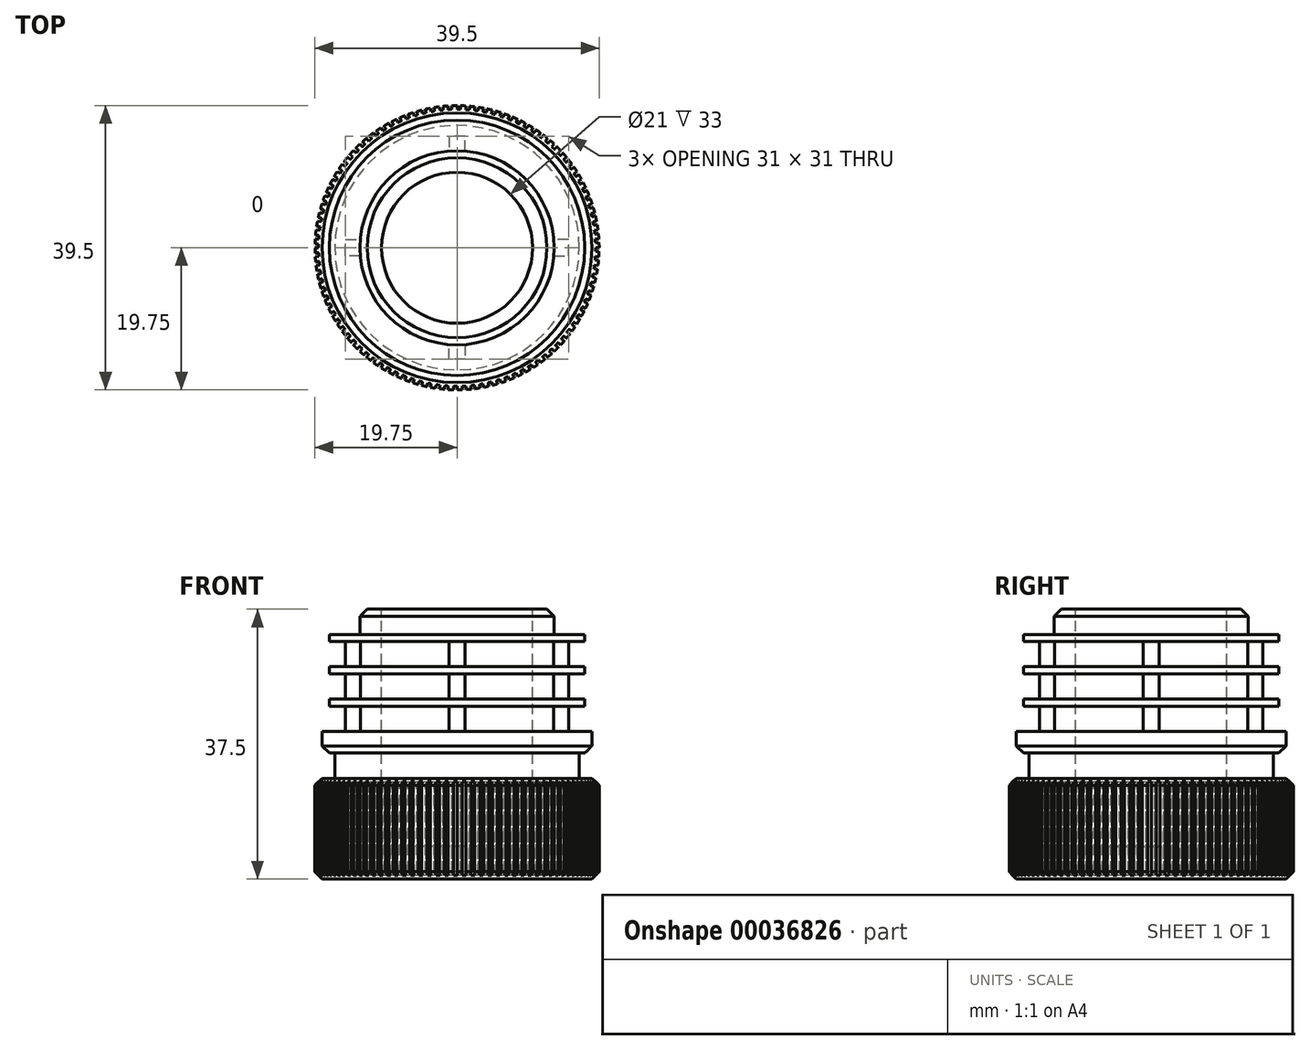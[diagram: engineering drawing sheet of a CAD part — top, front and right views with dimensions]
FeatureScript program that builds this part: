
annotation { "Feature Type Name" : "Feature", "Feature Type Description" : "" }
export const myFeature = defineFeature(function(context is Context, id is Id, definition is map)
    precondition{}
    {
        {
            var Q0;
            Q0=qCreatedBy(makeId("Front.planeOp"),FACE);
            var sketch = newSketch(context, id + "F0", { "sketchPlane" : qUnion([Q0])});
            skLineSegment(sketch, "E0", {"start": v(0, 48.86) * mm, "end": v(0, -30.6) * mm, "construction": true});
            skLineSegment(sketch, "E1", {"start": v(19.75, 0) * mm, "end": v(19.75, 14) * mm});
            skLineSegment(sketch, "E2", {"start": v(19.75, 14) * mm, "end": v(17, 14) * mm});
            skLineSegment(sketch, "E3", {"start": v(17, 14) * mm, "end": v(17, 17.5) * mm});
            skLineSegment(sketch, "E4", {"start": v(17, 17.5) * mm, "end": v(18.75, 17.5) * mm});
            skLineSegment(sketch, "E5", {"start": v(18.75, 17.5) * mm, "end": v(18.75, 20.5) * mm});
            skLineSegment(sketch, "E6", {"start": v(18.75, 20.5) * mm, "end": v(13.5, 20.5) * mm});
            skLineSegment(sketch, "E7", {"start": v(13.5, 20.5) * mm, "end": v(13.5, 24) * mm});
            skLineSegment(sketch, "E8", {"start": v(13.5, 24) * mm, "end": v(17.75, 24) * mm});
            skLineSegment(sketch, "E9", {"start": v(17.75, 24) * mm, "end": v(17.75, 25) * mm});
            skLineSegment(sketch, "E10", {"start": v(17.75, 25) * mm, "end": v(13.5, 25) * mm});
            skLineSegment(sketch, "E11", {"start": v(13.5, 25) * mm, "end": v(13.5, 28.5) * mm});
            skLineSegment(sketch, "E12", {"start": v(13.5, 28.5) * mm, "end": v(17.75, 28.5) * mm});
            skLineSegment(sketch, "E13", {"start": v(17.75, 28.5) * mm, "end": v(17.75, 29.5) * mm});
            skLineSegment(sketch, "E14", {"start": v(17.75, 29.5) * mm, "end": v(13.5, 29.5) * mm});
            skLineSegment(sketch, "E15", {"start": v(13.5, 29.5) * mm, "end": v(13.5, 33) * mm});
            skLineSegment(sketch, "E16", {"start": v(13.5, 33) * mm, "end": v(17.75, 33) * mm});
            skLineSegment(sketch, "E17", {"start": v(17.75, 33) * mm, "end": v(17.75, 34) * mm});
            skLineSegment(sketch, "E18", {"start": v(17.75, 34) * mm, "end": v(13.5, 34) * mm});
            skLineSegment(sketch, "E19", {"start": v(13.5, 34) * mm, "end": v(13.5, 37.5) * mm});
            skLineSegment(sketch, "E20", {"start": v(13.5, 37.5) * mm, "end": v(0, 37.5) * mm});
            skLineSegment(sketch, "E21", {"start": v(0, 37.5) * mm, "end": v(0, 0) * mm});
            skLineSegment(sketch, "E22", {"start": v(0, 0) * mm, "end": v(19.75, 0) * mm});
            skSolve(sketch);
        }
        {
            var Q0;
            Q0=makeQuery(id+"F0.imprint","IMPRINT",FACE,{"disambiguationData":[TD([[makeQuery(id+"F0.imprint","IMPRINT",EDGE,{"derivedFrom":sQuery(id+"F0.wireOp",EDGE,"E1")}),1.0]])]});
            var Q1;
            Q1=sQuery(id+"F0.wireOp",EDGE,"E21");
            revolve(context, id + "F1", {"entities" : qUnion([Q0]), "axis" : qUnion([Q1]), "revolveType" : RevolveType.FULL});
        }
        {
            var Q0;
            Q0=makeQuery(id+"F1.opRevolve","SWEPT_FACE",FACE,{"disambiguationData":[OSD([sQuery(id+"F0.wireOp",EDGE,"E20")])]});
            var sketch = newSketch(context, id + "F2", { "sketchPlane" : qUnion([Q0])});
            skCircle(sketch, "E23.0", {"center": v(0, 0) * mm, "radius": 13.5 * mm});
            skCircle(sketch, "E24.1", {"center": v(0, 0) * mm, "radius": 19.75 * mm});
            skLineSegment(sketch, "E25", {"start": v(-1.12, -13.45) * mm, "end": v(-1.12, -15.5) * mm});
            skLineSegment(sketch, "E26", {"start": v(-1.12, -15.5) * mm, "end": v(1.13, -15.5) * mm});
            skLineSegment(sketch, "E27", {"start": v(1.13, -15.5) * mm, "end": v(1.13, -13.45) * mm});
            skLineSegment(sketch, "E28", {"start": v(-35.88, 0) * mm, "end": v(36.7, 0) * mm, "construction": true});
            skLineSegment(sketch, "E29", {"start": v(0, 33.46) * mm, "end": v(0, -30.14) * mm, "construction": true});
            skPoint(sketch, "E30", {"position": v(0, -15.5) * mm});
            skLineSegment(sketch, "E31.MirrorCS", {"start": v(-1.13, 13.45) * mm, "end": v(-1.13, 15.5) * mm});
            skLineSegment(sketch, "E32.MirrorCS", {"start": v(1.12, 15.5) * mm, "end": v(1.12, 13.45) * mm});
            skLineSegment(sketch, "E33.MirrorCS", {"start": v(-1.12, 15.5) * mm, "end": v(1.13, 15.5) * mm});
            skLineSegment(sketch, "E34.1.0", {"start": v(-13.45, 1.12) * mm, "end": v(-15.5, 1.12) * mm});
            skLineSegment(sketch, "E34.1.1", {"start": v(-15.5, 1.12) * mm, "end": v(-15.5, -1.13) * mm});
            skLineSegment(sketch, "E34.1.2", {"start": v(-15.5, -1.13) * mm, "end": v(-13.45, -1.13) * mm});
            skLineSegment(sketch, "E34.1.3", {"start": v(15.5, 1.12) * mm, "end": v(15.5, -1.13) * mm});
            skLineSegment(sketch, "E34.1.4", {"start": v(13.45, 1.13) * mm, "end": v(15.5, 1.13) * mm});
            skLineSegment(sketch, "E34.1.5", {"start": v(15.5, -1.12) * mm, "end": v(13.45, -1.12) * mm});
            skLineSegment(sketch, "E34.anchor1", {"start": v(0, 0) * mm, "end": v(-1.12, -15.5) * mm, "construction": true});
            skLineSegment(sketch, "E34.anchor2", {"start": v(0, 0) * mm, "end": v(-15.5, 1.12) * mm, "construction": true});
            skLineSegment(sketch, "E35", {"start": v(0, -19.75) * mm, "end": v(0, -19.25) * mm});
            skLineSegment(sketch, "E36", {"start": v(0, -19.25) * mm, "end": v(-0.5, -19.25) * mm});
            skLineSegment(sketch, "E37", {"start": v(-0.5, -19.25) * mm, "end": v(-0.5, -19.74) * mm});
            skLineSegment(sketch, "E38.1.0", {"start": v(0.7, -19.24) * mm, "end": v(0.74, -19.74) * mm});
            skLineSegment(sketch, "E38.1.1", {"start": v(1.2, -19.21) * mm, "end": v(0.7, -19.24) * mm});
            skLineSegment(sketch, "E38.1.2", {"start": v(1.24, -19.71) * mm, "end": v(1.2, -19.21) * mm});
            skLineSegment(sketch, "E38.2.0", {"start": v(1.92, -19.16) * mm, "end": v(1.98, -19.65) * mm});
            skLineSegment(sketch, "E38.2.1", {"start": v(2.41, -19.1) * mm, "end": v(1.92, -19.16) * mm});
            skLineSegment(sketch, "E38.2.2", {"start": v(2.48, -19.6) * mm, "end": v(2.41, -19.1) * mm});
            skLineSegment(sketch, "E38.3.0", {"start": v(3.12, -19) * mm, "end": v(3.2, -19.49) * mm});
            skLineSegment(sketch, "E38.3.1", {"start": v(3.6, -18.9) * mm, "end": v(3.12, -19) * mm});
            skLineSegment(sketch, "E38.3.2", {"start": v(3.7, -19.4) * mm, "end": v(3.6, -18.9) * mm});
            skLineSegment(sketch, "E38.4.0", {"start": v(4.3, -18.77) * mm, "end": v(4.43, -19.25) * mm});
            skLineSegment(sketch, "E38.4.1", {"start": v(4.79, -18.65) * mm, "end": v(4.3, -18.77) * mm});
            skLineSegment(sketch, "E38.4.2", {"start": v(4.91, -19.13) * mm, "end": v(4.79, -18.65) * mm});
            skLineSegment(sketch, "E38.5.0", {"start": v(5.47, -18.46) * mm, "end": v(5.63, -18.93) * mm});
            skLineSegment(sketch, "E38.5.1", {"start": v(5.95, -18.3) * mm, "end": v(5.47, -18.46) * mm});
            skLineSegment(sketch, "E38.5.2", {"start": v(6.1, -18.78) * mm, "end": v(5.95, -18.3) * mm});
            skLineSegment(sketch, "E38.6.0", {"start": v(6.62, -18.08) * mm, "end": v(6.8, -18.54) * mm});
            skLineSegment(sketch, "E38.6.1", {"start": v(7.09, -17.9) * mm, "end": v(6.62, -18.08) * mm});
            skLineSegment(sketch, "E38.6.2", {"start": v(7.27, -18.36) * mm, "end": v(7.09, -17.9) * mm});
            skLineSegment(sketch, "E38.7.0", {"start": v(7.74, -17.63) * mm, "end": v(7.95, -18.08) * mm});
            skLineSegment(sketch, "E38.7.1", {"start": v(8.2, -17.42) * mm, "end": v(7.74, -17.63) * mm});
            skLineSegment(sketch, "E38.7.2", {"start": v(8.4, -17.87) * mm, "end": v(8.2, -17.42) * mm});
            skLineSegment(sketch, "E38.8.0", {"start": v(8.84, -17.1) * mm, "end": v(9.07, -17.54) * mm});
            skLineSegment(sketch, "E38.8.1", {"start": v(9.27, -16.87) * mm, "end": v(8.84, -17.1) * mm});
            skLineSegment(sketch, "E38.8.2", {"start": v(9.51, -17.3) * mm, "end": v(9.27, -16.87) * mm});
            skLineSegment(sketch, "E38.9.0", {"start": v(9.9, -16.52) * mm, "end": v(10.16, -16.94) * mm});
            skLineSegment(sketch, "E38.9.1", {"start": v(10.31, -16.25) * mm, "end": v(9.9, -16.52) * mm});
            skLineSegment(sketch, "E38.9.2", {"start": v(10.58, -16.68) * mm, "end": v(10.31, -16.25) * mm});
            skLineSegment(sketch, "E38.10.0", {"start": v(10.91, -15.87) * mm, "end": v(11.2, -16.27) * mm});
            skLineSegment(sketch, "E38.10.1", {"start": v(11.31, -15.57) * mm, "end": v(10.91, -15.87) * mm});
            skLineSegment(sketch, "E38.10.2", {"start": v(11.6, -15.98) * mm, "end": v(11.31, -15.57) * mm});
            skLineSegment(sketch, "E38.11.0", {"start": v(11.89, -15.15) * mm, "end": v(12.2, -15.53) * mm});
            skLineSegment(sketch, "E38.11.1", {"start": v(12.27, -14.83) * mm, "end": v(11.89, -15.15) * mm});
            skLineSegment(sketch, "E38.11.2", {"start": v(12.59, -15.22) * mm, "end": v(12.27, -14.83) * mm});
            skLineSegment(sketch, "E38.12.0", {"start": v(12.81, -14.37) * mm, "end": v(13.15, -14.73) * mm});
            skLineSegment(sketch, "E38.12.1", {"start": v(13.18, -14.03) * mm, "end": v(12.81, -14.37) * mm});
            skLineSegment(sketch, "E38.12.2", {"start": v(13.52, -14.4) * mm, "end": v(13.18, -14.03) * mm});
            skLineSegment(sketch, "E38.13.0", {"start": v(13.7, -13.54) * mm, "end": v(14.05, -13.88) * mm});
            skLineSegment(sketch, "E38.13.1", {"start": v(14.03, -13.18) * mm, "end": v(13.7, -13.54) * mm});
            skLineSegment(sketch, "E38.13.2", {"start": v(14.4, -13.52) * mm, "end": v(14.03, -13.18) * mm});
            skLineSegment(sketch, "E38.14.0", {"start": v(14.51, -12.66) * mm, "end": v(14.9, -12.97) * mm});
            skLineSegment(sketch, "E38.14.1", {"start": v(14.83, -12.27) * mm, "end": v(14.51, -12.66) * mm});
            skLineSegment(sketch, "E38.14.2", {"start": v(15.22, -12.59) * mm, "end": v(14.83, -12.27) * mm});
            skLineSegment(sketch, "E38.15.0", {"start": v(15.28, -11.72) * mm, "end": v(15.68, -12) * mm});
            skLineSegment(sketch, "E38.15.1", {"start": v(15.57, -11.31) * mm, "end": v(15.28, -11.72) * mm});
            skLineSegment(sketch, "E38.15.2", {"start": v(15.98, -11.6) * mm, "end": v(15.57, -11.31) * mm});
            skLineSegment(sketch, "E38.16.0", {"start": v(15.99, -10.74) * mm, "end": v(16.4, -11) * mm});
            skLineSegment(sketch, "E38.16.1", {"start": v(16.25, -10.31) * mm, "end": v(15.99, -10.74) * mm});
            skLineSegment(sketch, "E38.16.2", {"start": v(16.68, -10.58) * mm, "end": v(16.25, -10.31) * mm});
            skLineSegment(sketch, "E38.17.0", {"start": v(16.63, -9.71) * mm, "end": v(17.06, -9.95) * mm});
            skLineSegment(sketch, "E38.17.1", {"start": v(16.87, -9.27) * mm, "end": v(16.63, -9.71) * mm});
            skLineSegment(sketch, "E38.17.2", {"start": v(17.3, -9.51) * mm, "end": v(16.87, -9.27) * mm});
            skLineSegment(sketch, "E38.18.0", {"start": v(17.2, -8.65) * mm, "end": v(17.65, -8.86) * mm});
            skLineSegment(sketch, "E38.18.1", {"start": v(17.42, -8.2) * mm, "end": v(17.2, -8.65) * mm});
            skLineSegment(sketch, "E38.18.2", {"start": v(17.87, -8.4) * mm, "end": v(17.42, -8.2) * mm});
            skLineSegment(sketch, "E38.19.0", {"start": v(17.71, -7.55) * mm, "end": v(18.17, -7.73) * mm});
            skLineSegment(sketch, "E38.19.1", {"start": v(17.9, -7.09) * mm, "end": v(17.71, -7.55) * mm});
            skLineSegment(sketch, "E38.19.2", {"start": v(18.36, -7.27) * mm, "end": v(17.9, -7.09) * mm});
            skLineSegment(sketch, "E38.20.0", {"start": v(18.15, -6.42) * mm, "end": v(18.62, -6.58) * mm});
            skLineSegment(sketch, "E38.20.1", {"start": v(18.3, -5.95) * mm, "end": v(18.15, -6.42) * mm});
            skLineSegment(sketch, "E38.20.2", {"start": v(18.78, -6.1) * mm, "end": v(18.3, -5.95) * mm});
            skLineSegment(sketch, "E38.21.0", {"start": v(18.52, -5.27) * mm, "end": v(19, -5.4) * mm});
            skLineSegment(sketch, "E38.21.1", {"start": v(18.65, -4.79) * mm, "end": v(18.52, -5.27) * mm});
            skLineSegment(sketch, "E38.21.2", {"start": v(19.13, -4.91) * mm, "end": v(18.65, -4.79) * mm});
            skLineSegment(sketch, "E38.22.0", {"start": v(18.82, -4.1) * mm, "end": v(19.3, -4.2) * mm});
            skLineSegment(sketch, "E38.22.1", {"start": v(18.9, -3.6) * mm, "end": v(18.82, -4.1) * mm});
            skLineSegment(sketch, "E38.22.2", {"start": v(19.4, -3.7) * mm, "end": v(18.9, -3.6) * mm});
            skLineSegment(sketch, "E38.23.0", {"start": v(19.04, -2.9) * mm, "end": v(19.53, -2.97) * mm});
            skLineSegment(sketch, "E38.23.1", {"start": v(19.1, -2.41) * mm, "end": v(19.04, -2.9) * mm});
            skLineSegment(sketch, "E38.23.2", {"start": v(19.6, -2.48) * mm, "end": v(19.1, -2.41) * mm});
            skLineSegment(sketch, "E38.24.0", {"start": v(19.18, -1.7) * mm, "end": v(19.67, -1.74) * mm});
            skLineSegment(sketch, "E38.24.1", {"start": v(19.21, -1.2) * mm, "end": v(19.18, -1.7) * mm});
            skLineSegment(sketch, "E38.24.2", {"start": v(19.71, -1.24) * mm, "end": v(19.21, -1.2) * mm});
            skLineSegment(sketch, "E38.25.0", {"start": v(19.25, -0.5) * mm, "end": v(19.74, -0.5) * mm});
            skLineSegment(sketch, "E38.25.1", {"start": v(19.25, 0) * mm, "end": v(19.25, -0.5) * mm});
            skLineSegment(sketch, "E38.25.2", {"start": v(19.75, 0) * mm, "end": v(19.25, 0) * mm});
            skLineSegment(sketch, "E38.26.0", {"start": v(19.24, 0.7) * mm, "end": v(19.74, 0.74) * mm});
            skLineSegment(sketch, "E38.26.1", {"start": v(19.21, 1.2) * mm, "end": v(19.24, 0.7) * mm});
            skLineSegment(sketch, "E38.26.2", {"start": v(19.71, 1.24) * mm, "end": v(19.21, 1.2) * mm});
            skLineSegment(sketch, "E38.27.0", {"start": v(19.16, 1.92) * mm, "end": v(19.65, 1.98) * mm});
            skLineSegment(sketch, "E38.27.1", {"start": v(19.1, 2.41) * mm, "end": v(19.16, 1.92) * mm});
            skLineSegment(sketch, "E38.27.2", {"start": v(19.6, 2.48) * mm, "end": v(19.1, 2.41) * mm});
            skLineSegment(sketch, "E38.28.0", {"start": v(19, 3.12) * mm, "end": v(19.49, 3.2) * mm});
            skLineSegment(sketch, "E38.28.1", {"start": v(18.9, 3.6) * mm, "end": v(19, 3.12) * mm});
            skLineSegment(sketch, "E38.28.2", {"start": v(19.4, 3.7) * mm, "end": v(18.9, 3.6) * mm});
            skLineSegment(sketch, "E38.29.0", {"start": v(18.77, 4.3) * mm, "end": v(19.25, 4.43) * mm});
            skLineSegment(sketch, "E38.29.1", {"start": v(18.65, 4.79) * mm, "end": v(18.77, 4.3) * mm});
            skLineSegment(sketch, "E38.29.2", {"start": v(19.13, 4.91) * mm, "end": v(18.65, 4.79) * mm});
            skLineSegment(sketch, "E38.30.0", {"start": v(18.46, 5.47) * mm, "end": v(18.93, 5.63) * mm});
            skLineSegment(sketch, "E38.30.1", {"start": v(18.3, 5.95) * mm, "end": v(18.46, 5.47) * mm});
            skLineSegment(sketch, "E38.30.2", {"start": v(18.78, 6.1) * mm, "end": v(18.3, 5.95) * mm});
            skLineSegment(sketch, "E38.31.0", {"start": v(18.08, 6.62) * mm, "end": v(18.54, 6.8) * mm});
            skLineSegment(sketch, "E38.31.1", {"start": v(17.9, 7.09) * mm, "end": v(18.08, 6.62) * mm});
            skLineSegment(sketch, "E38.31.2", {"start": v(18.36, 7.27) * mm, "end": v(17.9, 7.09) * mm});
            skLineSegment(sketch, "E38.32.0", {"start": v(17.63, 7.74) * mm, "end": v(18.08, 7.95) * mm});
            skLineSegment(sketch, "E38.32.1", {"start": v(17.42, 8.2) * mm, "end": v(17.63, 7.74) * mm});
            skLineSegment(sketch, "E38.32.2", {"start": v(17.87, 8.4) * mm, "end": v(17.42, 8.2) * mm});
            skLineSegment(sketch, "E38.33.0", {"start": v(17.1, 8.84) * mm, "end": v(17.54, 9.07) * mm});
            skLineSegment(sketch, "E38.33.1", {"start": v(16.87, 9.27) * mm, "end": v(17.1, 8.84) * mm});
            skLineSegment(sketch, "E38.33.2", {"start": v(17.3, 9.51) * mm, "end": v(16.87, 9.27) * mm});
            skLineSegment(sketch, "E38.34.0", {"start": v(16.52, 9.9) * mm, "end": v(16.94, 10.16) * mm});
            skLineSegment(sketch, "E38.34.1", {"start": v(16.25, 10.31) * mm, "end": v(16.52, 9.9) * mm});
            skLineSegment(sketch, "E38.34.2", {"start": v(16.68, 10.58) * mm, "end": v(16.25, 10.31) * mm});
            skLineSegment(sketch, "E38.35.0", {"start": v(15.87, 10.91) * mm, "end": v(16.27, 11.2) * mm});
            skLineSegment(sketch, "E38.35.1", {"start": v(15.57, 11.31) * mm, "end": v(15.87, 10.91) * mm});
            skLineSegment(sketch, "E38.35.2", {"start": v(15.98, 11.6) * mm, "end": v(15.57, 11.31) * mm});
            skLineSegment(sketch, "E38.36.0", {"start": v(15.15, 11.89) * mm, "end": v(15.53, 12.2) * mm});
            skLineSegment(sketch, "E38.36.1", {"start": v(14.83, 12.27) * mm, "end": v(15.15, 11.89) * mm});
            skLineSegment(sketch, "E38.36.2", {"start": v(15.22, 12.59) * mm, "end": v(14.83, 12.27) * mm});
            skLineSegment(sketch, "E38.37.0", {"start": v(14.37, 12.81) * mm, "end": v(14.73, 13.15) * mm});
            skLineSegment(sketch, "E38.37.1", {"start": v(14.03, 13.18) * mm, "end": v(14.37, 12.81) * mm});
            skLineSegment(sketch, "E38.37.2", {"start": v(14.4, 13.52) * mm, "end": v(14.03, 13.18) * mm});
            skLineSegment(sketch, "E38.38.0", {"start": v(13.54, 13.7) * mm, "end": v(13.88, 14.05) * mm});
            skLineSegment(sketch, "E38.38.1", {"start": v(13.18, 14.03) * mm, "end": v(13.54, 13.7) * mm});
            skLineSegment(sketch, "E38.38.2", {"start": v(13.52, 14.4) * mm, "end": v(13.18, 14.03) * mm});
            skLineSegment(sketch, "E38.39.0", {"start": v(12.66, 14.51) * mm, "end": v(12.97, 14.9) * mm});
            skLineSegment(sketch, "E38.39.1", {"start": v(12.27, 14.83) * mm, "end": v(12.66, 14.51) * mm});
            skLineSegment(sketch, "E38.39.2", {"start": v(12.59, 15.22) * mm, "end": v(12.27, 14.83) * mm});
            skLineSegment(sketch, "E38.40.0", {"start": v(11.72, 15.28) * mm, "end": v(12, 15.68) * mm});
            skLineSegment(sketch, "E38.40.1", {"start": v(11.31, 15.57) * mm, "end": v(11.72, 15.28) * mm});
            skLineSegment(sketch, "E38.40.2", {"start": v(11.6, 15.98) * mm, "end": v(11.31, 15.57) * mm});
            skLineSegment(sketch, "E38.41.0", {"start": v(10.74, 15.99) * mm, "end": v(11, 16.4) * mm});
            skLineSegment(sketch, "E38.41.1", {"start": v(10.31, 16.25) * mm, "end": v(10.74, 15.99) * mm});
            skLineSegment(sketch, "E38.41.2", {"start": v(10.58, 16.68) * mm, "end": v(10.31, 16.25) * mm});
            skLineSegment(sketch, "E38.42.0", {"start": v(9.71, 16.63) * mm, "end": v(9.95, 17.06) * mm});
            skLineSegment(sketch, "E38.42.1", {"start": v(9.27, 16.87) * mm, "end": v(9.71, 16.63) * mm});
            skLineSegment(sketch, "E38.42.2", {"start": v(9.51, 17.3) * mm, "end": v(9.27, 16.87) * mm});
            skLineSegment(sketch, "E38.43.0", {"start": v(8.65, 17.2) * mm, "end": v(8.86, 17.65) * mm});
            skLineSegment(sketch, "E38.43.1", {"start": v(8.2, 17.42) * mm, "end": v(8.65, 17.2) * mm});
            skLineSegment(sketch, "E38.43.2", {"start": v(8.4, 17.87) * mm, "end": v(8.2, 17.42) * mm});
            skLineSegment(sketch, "E38.44.0", {"start": v(7.55, 17.71) * mm, "end": v(7.73, 18.17) * mm});
            skLineSegment(sketch, "E38.44.1", {"start": v(7.09, 17.9) * mm, "end": v(7.55, 17.71) * mm});
            skLineSegment(sketch, "E38.44.2", {"start": v(7.27, 18.36) * mm, "end": v(7.09, 17.9) * mm});
            skLineSegment(sketch, "E38.45.0", {"start": v(6.42, 18.15) * mm, "end": v(6.58, 18.62) * mm});
            skLineSegment(sketch, "E38.45.1", {"start": v(5.95, 18.3) * mm, "end": v(6.42, 18.15) * mm});
            skLineSegment(sketch, "E38.45.2", {"start": v(6.1, 18.78) * mm, "end": v(5.95, 18.3) * mm});
            skLineSegment(sketch, "E38.46.0", {"start": v(5.27, 18.52) * mm, "end": v(5.4, 19) * mm});
            skLineSegment(sketch, "E38.46.1", {"start": v(4.79, 18.65) * mm, "end": v(5.27, 18.52) * mm});
            skLineSegment(sketch, "E38.46.2", {"start": v(4.91, 19.13) * mm, "end": v(4.79, 18.65) * mm});
            skLineSegment(sketch, "E38.47.0", {"start": v(4.1, 18.82) * mm, "end": v(4.2, 19.3) * mm});
            skLineSegment(sketch, "E38.47.1", {"start": v(3.6, 18.9) * mm, "end": v(4.1, 18.82) * mm});
            skLineSegment(sketch, "E38.47.2", {"start": v(3.7, 19.4) * mm, "end": v(3.6, 18.9) * mm});
            skLineSegment(sketch, "E38.48.0", {"start": v(2.9, 19.04) * mm, "end": v(2.97, 19.53) * mm});
            skLineSegment(sketch, "E38.48.1", {"start": v(2.41, 19.1) * mm, "end": v(2.9, 19.04) * mm});
            skLineSegment(sketch, "E38.48.2", {"start": v(2.48, 19.6) * mm, "end": v(2.41, 19.1) * mm});
            skLineSegment(sketch, "E38.49.0", {"start": v(1.7, 19.18) * mm, "end": v(1.74, 19.67) * mm});
            skLineSegment(sketch, "E38.49.1", {"start": v(1.2, 19.21) * mm, "end": v(1.7, 19.18) * mm});
            skLineSegment(sketch, "E38.49.2", {"start": v(1.24, 19.71) * mm, "end": v(1.2, 19.21) * mm});
            skLineSegment(sketch, "E38.50.0", {"start": v(0.5, 19.25) * mm, "end": v(0.5, 19.74) * mm});
            skLineSegment(sketch, "E38.50.1", {"start": v(0, 19.25) * mm, "end": v(0.5, 19.25) * mm});
            skLineSegment(sketch, "E38.50.2", {"start": v(0, 19.75) * mm, "end": v(0, 19.25) * mm});
            skLineSegment(sketch, "E38.51.0", {"start": v(-0.7, 19.24) * mm, "end": v(-0.74, 19.74) * mm});
            skLineSegment(sketch, "E38.51.1", {"start": v(-1.2, 19.21) * mm, "end": v(-0.7, 19.24) * mm});
            skLineSegment(sketch, "E38.51.2", {"start": v(-1.24, 19.71) * mm, "end": v(-1.2, 19.21) * mm});
            skLineSegment(sketch, "E38.52.0", {"start": v(-1.92, 19.16) * mm, "end": v(-1.98, 19.65) * mm});
            skLineSegment(sketch, "E38.52.1", {"start": v(-2.41, 19.1) * mm, "end": v(-1.92, 19.16) * mm});
            skLineSegment(sketch, "E38.52.2", {"start": v(-2.48, 19.6) * mm, "end": v(-2.41, 19.1) * mm});
            skLineSegment(sketch, "E38.53.0", {"start": v(-3.12, 19) * mm, "end": v(-3.2, 19.49) * mm});
            skLineSegment(sketch, "E38.53.1", {"start": v(-3.6, 18.9) * mm, "end": v(-3.12, 19) * mm});
            skLineSegment(sketch, "E38.53.2", {"start": v(-3.7, 19.4) * mm, "end": v(-3.6, 18.9) * mm});
            skLineSegment(sketch, "E38.54.0", {"start": v(-4.3, 18.77) * mm, "end": v(-4.43, 19.25) * mm});
            skLineSegment(sketch, "E38.54.1", {"start": v(-4.79, 18.65) * mm, "end": v(-4.3, 18.77) * mm});
            skLineSegment(sketch, "E38.54.2", {"start": v(-4.91, 19.13) * mm, "end": v(-4.79, 18.65) * mm});
            skLineSegment(sketch, "E38.55.0", {"start": v(-5.47, 18.46) * mm, "end": v(-5.63, 18.93) * mm});
            skLineSegment(sketch, "E38.55.1", {"start": v(-5.95, 18.3) * mm, "end": v(-5.47, 18.46) * mm});
            skLineSegment(sketch, "E38.55.2", {"start": v(-6.1, 18.78) * mm, "end": v(-5.95, 18.3) * mm});
            skLineSegment(sketch, "E38.56.0", {"start": v(-6.62, 18.08) * mm, "end": v(-6.8, 18.54) * mm});
            skLineSegment(sketch, "E38.56.1", {"start": v(-7.09, 17.9) * mm, "end": v(-6.62, 18.08) * mm});
            skLineSegment(sketch, "E38.56.2", {"start": v(-7.27, 18.36) * mm, "end": v(-7.09, 17.9) * mm});
            skLineSegment(sketch, "E38.57.0", {"start": v(-7.74, 17.63) * mm, "end": v(-7.95, 18.08) * mm});
            skLineSegment(sketch, "E38.57.1", {"start": v(-8.2, 17.42) * mm, "end": v(-7.74, 17.63) * mm});
            skLineSegment(sketch, "E38.57.2", {"start": v(-8.4, 17.87) * mm, "end": v(-8.2, 17.42) * mm});
            skLineSegment(sketch, "E38.58.0", {"start": v(-8.84, 17.1) * mm, "end": v(-9.07, 17.54) * mm});
            skLineSegment(sketch, "E38.58.1", {"start": v(-9.27, 16.87) * mm, "end": v(-8.84, 17.1) * mm});
            skLineSegment(sketch, "E38.58.2", {"start": v(-9.51, 17.3) * mm, "end": v(-9.27, 16.87) * mm});
            skLineSegment(sketch, "E38.59.0", {"start": v(-9.9, 16.52) * mm, "end": v(-10.16, 16.94) * mm});
            skLineSegment(sketch, "E38.59.1", {"start": v(-10.31, 16.25) * mm, "end": v(-9.9, 16.52) * mm});
            skLineSegment(sketch, "E38.59.2", {"start": v(-10.58, 16.68) * mm, "end": v(-10.31, 16.25) * mm});
            skLineSegment(sketch, "E38.60.0", {"start": v(-10.91, 15.87) * mm, "end": v(-11.2, 16.27) * mm});
            skLineSegment(sketch, "E38.60.1", {"start": v(-11.31, 15.57) * mm, "end": v(-10.91, 15.87) * mm});
            skLineSegment(sketch, "E38.60.2", {"start": v(-11.6, 15.98) * mm, "end": v(-11.31, 15.57) * mm});
            skLineSegment(sketch, "E38.61.0", {"start": v(-11.89, 15.15) * mm, "end": v(-12.2, 15.53) * mm});
            skLineSegment(sketch, "E38.61.1", {"start": v(-12.27, 14.83) * mm, "end": v(-11.89, 15.15) * mm});
            skLineSegment(sketch, "E38.61.2", {"start": v(-12.59, 15.22) * mm, "end": v(-12.27, 14.83) * mm});
            skLineSegment(sketch, "E38.62.0", {"start": v(-12.81, 14.37) * mm, "end": v(-13.15, 14.73) * mm});
            skLineSegment(sketch, "E38.62.1", {"start": v(-13.18, 14.03) * mm, "end": v(-12.81, 14.37) * mm});
            skLineSegment(sketch, "E38.62.2", {"start": v(-13.52, 14.4) * mm, "end": v(-13.18, 14.03) * mm});
            skLineSegment(sketch, "E38.63.0", {"start": v(-13.7, 13.54) * mm, "end": v(-14.05, 13.88) * mm});
            skLineSegment(sketch, "E38.63.1", {"start": v(-14.03, 13.18) * mm, "end": v(-13.7, 13.54) * mm});
            skLineSegment(sketch, "E38.63.2", {"start": v(-14.4, 13.52) * mm, "end": v(-14.03, 13.18) * mm});
            skLineSegment(sketch, "E38.64.0", {"start": v(-14.51, 12.66) * mm, "end": v(-14.9, 12.97) * mm});
            skLineSegment(sketch, "E38.64.1", {"start": v(-14.83, 12.27) * mm, "end": v(-14.51, 12.66) * mm});
            skLineSegment(sketch, "E38.64.2", {"start": v(-15.22, 12.59) * mm, "end": v(-14.83, 12.27) * mm});
            skLineSegment(sketch, "E38.65.0", {"start": v(-15.28, 11.72) * mm, "end": v(-15.68, 12) * mm});
            skLineSegment(sketch, "E38.65.1", {"start": v(-15.57, 11.31) * mm, "end": v(-15.28, 11.72) * mm});
            skLineSegment(sketch, "E38.65.2", {"start": v(-15.98, 11.6) * mm, "end": v(-15.57, 11.31) * mm});
            skLineSegment(sketch, "E38.66.0", {"start": v(-15.99, 10.74) * mm, "end": v(-16.4, 11) * mm});
            skLineSegment(sketch, "E38.66.1", {"start": v(-16.25, 10.31) * mm, "end": v(-15.99, 10.74) * mm});
            skLineSegment(sketch, "E38.66.2", {"start": v(-16.68, 10.58) * mm, "end": v(-16.25, 10.31) * mm});
            skLineSegment(sketch, "E38.67.0", {"start": v(-16.63, 9.71) * mm, "end": v(-17.06, 9.95) * mm});
            skLineSegment(sketch, "E38.67.1", {"start": v(-16.87, 9.27) * mm, "end": v(-16.63, 9.71) * mm});
            skLineSegment(sketch, "E38.67.2", {"start": v(-17.3, 9.51) * mm, "end": v(-16.87, 9.27) * mm});
            skLineSegment(sketch, "E38.68.0", {"start": v(-17.2, 8.65) * mm, "end": v(-17.65, 8.86) * mm});
            skLineSegment(sketch, "E38.68.1", {"start": v(-17.42, 8.2) * mm, "end": v(-17.2, 8.65) * mm});
            skLineSegment(sketch, "E38.68.2", {"start": v(-17.87, 8.4) * mm, "end": v(-17.42, 8.2) * mm});
            skLineSegment(sketch, "E38.69.0", {"start": v(-17.71, 7.55) * mm, "end": v(-18.17, 7.73) * mm});
            skLineSegment(sketch, "E38.69.1", {"start": v(-17.9, 7.09) * mm, "end": v(-17.71, 7.55) * mm});
            skLineSegment(sketch, "E38.69.2", {"start": v(-18.36, 7.27) * mm, "end": v(-17.9, 7.09) * mm});
            skLineSegment(sketch, "E38.70.0", {"start": v(-18.15, 6.42) * mm, "end": v(-18.62, 6.58) * mm});
            skLineSegment(sketch, "E38.70.1", {"start": v(-18.3, 5.95) * mm, "end": v(-18.15, 6.42) * mm});
            skLineSegment(sketch, "E38.70.2", {"start": v(-18.78, 6.1) * mm, "end": v(-18.3, 5.95) * mm});
            skLineSegment(sketch, "E38.71.0", {"start": v(-18.52, 5.27) * mm, "end": v(-19, 5.4) * mm});
            skLineSegment(sketch, "E38.71.1", {"start": v(-18.65, 4.79) * mm, "end": v(-18.52, 5.27) * mm});
            skLineSegment(sketch, "E38.71.2", {"start": v(-19.13, 4.91) * mm, "end": v(-18.65, 4.79) * mm});
            skLineSegment(sketch, "E38.72.0", {"start": v(-18.82, 4.1) * mm, "end": v(-19.3, 4.2) * mm});
            skLineSegment(sketch, "E38.72.1", {"start": v(-18.9, 3.6) * mm, "end": v(-18.82, 4.1) * mm});
            skLineSegment(sketch, "E38.72.2", {"start": v(-19.4, 3.7) * mm, "end": v(-18.9, 3.6) * mm});
            skLineSegment(sketch, "E38.73.0", {"start": v(-19.04, 2.9) * mm, "end": v(-19.53, 2.97) * mm});
            skLineSegment(sketch, "E38.73.1", {"start": v(-19.1, 2.41) * mm, "end": v(-19.04, 2.9) * mm});
            skLineSegment(sketch, "E38.73.2", {"start": v(-19.6, 2.48) * mm, "end": v(-19.1, 2.41) * mm});
            skLineSegment(sketch, "E38.74.0", {"start": v(-19.18, 1.7) * mm, "end": v(-19.67, 1.74) * mm});
            skLineSegment(sketch, "E38.74.1", {"start": v(-19.21, 1.2) * mm, "end": v(-19.18, 1.7) * mm});
            skLineSegment(sketch, "E38.74.2", {"start": v(-19.71, 1.24) * mm, "end": v(-19.21, 1.2) * mm});
            skLineSegment(sketch, "E38.75.0", {"start": v(-19.25, 0.5) * mm, "end": v(-19.74, 0.5) * mm});
            skLineSegment(sketch, "E38.75.1", {"start": v(-19.25, 0) * mm, "end": v(-19.25, 0.5) * mm});
            skLineSegment(sketch, "E38.75.2", {"start": v(-19.75, 0) * mm, "end": v(-19.25, 0) * mm});
            skLineSegment(sketch, "E38.76.0", {"start": v(-19.24, -0.7) * mm, "end": v(-19.74, -0.74) * mm});
            skLineSegment(sketch, "E38.76.1", {"start": v(-19.21, -1.2) * mm, "end": v(-19.24, -0.7) * mm});
            skLineSegment(sketch, "E38.76.2", {"start": v(-19.71, -1.24) * mm, "end": v(-19.21, -1.2) * mm});
            skLineSegment(sketch, "E38.77.0", {"start": v(-19.16, -1.92) * mm, "end": v(-19.65, -1.98) * mm});
            skLineSegment(sketch, "E38.77.1", {"start": v(-19.1, -2.41) * mm, "end": v(-19.16, -1.92) * mm});
            skLineSegment(sketch, "E38.77.2", {"start": v(-19.6, -2.48) * mm, "end": v(-19.1, -2.41) * mm});
            skLineSegment(sketch, "E38.78.0", {"start": v(-19, -3.12) * mm, "end": v(-19.49, -3.2) * mm});
            skLineSegment(sketch, "E38.78.1", {"start": v(-18.9, -3.6) * mm, "end": v(-19, -3.12) * mm});
            skLineSegment(sketch, "E38.78.2", {"start": v(-19.4, -3.7) * mm, "end": v(-18.9, -3.6) * mm});
            skLineSegment(sketch, "E38.79.0", {"start": v(-18.77, -4.3) * mm, "end": v(-19.25, -4.43) * mm});
            skLineSegment(sketch, "E38.79.1", {"start": v(-18.65, -4.79) * mm, "end": v(-18.77, -4.3) * mm});
            skLineSegment(sketch, "E38.79.2", {"start": v(-19.13, -4.91) * mm, "end": v(-18.65, -4.79) * mm});
            skLineSegment(sketch, "E38.80.0", {"start": v(-18.46, -5.47) * mm, "end": v(-18.93, -5.63) * mm});
            skLineSegment(sketch, "E38.80.1", {"start": v(-18.3, -5.95) * mm, "end": v(-18.46, -5.47) * mm});
            skLineSegment(sketch, "E38.80.2", {"start": v(-18.78, -6.1) * mm, "end": v(-18.3, -5.95) * mm});
            skLineSegment(sketch, "E38.81.0", {"start": v(-18.08, -6.62) * mm, "end": v(-18.54, -6.8) * mm});
            skLineSegment(sketch, "E38.81.1", {"start": v(-17.9, -7.09) * mm, "end": v(-18.08, -6.62) * mm});
            skLineSegment(sketch, "E38.81.2", {"start": v(-18.36, -7.27) * mm, "end": v(-17.9, -7.09) * mm});
            skLineSegment(sketch, "E38.82.0", {"start": v(-17.63, -7.74) * mm, "end": v(-18.08, -7.95) * mm});
            skLineSegment(sketch, "E38.82.1", {"start": v(-17.42, -8.2) * mm, "end": v(-17.63, -7.74) * mm});
            skLineSegment(sketch, "E38.82.2", {"start": v(-17.87, -8.4) * mm, "end": v(-17.42, -8.2) * mm});
            skLineSegment(sketch, "E38.83.0", {"start": v(-17.1, -8.84) * mm, "end": v(-17.54, -9.07) * mm});
            skLineSegment(sketch, "E38.83.1", {"start": v(-16.87, -9.27) * mm, "end": v(-17.1, -8.84) * mm});
            skLineSegment(sketch, "E38.83.2", {"start": v(-17.3, -9.51) * mm, "end": v(-16.87, -9.27) * mm});
            skLineSegment(sketch, "E38.84.0", {"start": v(-16.52, -9.9) * mm, "end": v(-16.94, -10.16) * mm});
            skLineSegment(sketch, "E38.84.1", {"start": v(-16.25, -10.31) * mm, "end": v(-16.52, -9.9) * mm});
            skLineSegment(sketch, "E38.84.2", {"start": v(-16.68, -10.58) * mm, "end": v(-16.25, -10.31) * mm});
            skLineSegment(sketch, "E38.85.0", {"start": v(-15.87, -10.91) * mm, "end": v(-16.27, -11.2) * mm});
            skLineSegment(sketch, "E38.85.1", {"start": v(-15.57, -11.31) * mm, "end": v(-15.87, -10.91) * mm});
            skLineSegment(sketch, "E38.85.2", {"start": v(-15.98, -11.6) * mm, "end": v(-15.57, -11.31) * mm});
            skLineSegment(sketch, "E38.86.0", {"start": v(-15.15, -11.89) * mm, "end": v(-15.53, -12.2) * mm});
            skLineSegment(sketch, "E38.86.1", {"start": v(-14.83, -12.27) * mm, "end": v(-15.15, -11.89) * mm});
            skLineSegment(sketch, "E38.86.2", {"start": v(-15.22, -12.59) * mm, "end": v(-14.83, -12.27) * mm});
            skLineSegment(sketch, "E38.87.0", {"start": v(-14.37, -12.81) * mm, "end": v(-14.73, -13.15) * mm});
            skLineSegment(sketch, "E38.87.1", {"start": v(-14.03, -13.18) * mm, "end": v(-14.37, -12.81) * mm});
            skLineSegment(sketch, "E38.87.2", {"start": v(-14.4, -13.52) * mm, "end": v(-14.03, -13.18) * mm});
            skLineSegment(sketch, "E38.88.0", {"start": v(-13.54, -13.7) * mm, "end": v(-13.88, -14.05) * mm});
            skLineSegment(sketch, "E38.88.1", {"start": v(-13.18, -14.03) * mm, "end": v(-13.54, -13.7) * mm});
            skLineSegment(sketch, "E38.88.2", {"start": v(-13.52, -14.4) * mm, "end": v(-13.18, -14.03) * mm});
            skLineSegment(sketch, "E38.89.0", {"start": v(-12.66, -14.51) * mm, "end": v(-12.97, -14.9) * mm});
            skLineSegment(sketch, "E38.89.1", {"start": v(-12.27, -14.83) * mm, "end": v(-12.66, -14.51) * mm});
            skLineSegment(sketch, "E38.89.2", {"start": v(-12.59, -15.22) * mm, "end": v(-12.27, -14.83) * mm});
            skLineSegment(sketch, "E38.90.0", {"start": v(-11.72, -15.28) * mm, "end": v(-12, -15.68) * mm});
            skLineSegment(sketch, "E38.90.1", {"start": v(-11.31, -15.57) * mm, "end": v(-11.72, -15.28) * mm});
            skLineSegment(sketch, "E38.90.2", {"start": v(-11.6, -15.98) * mm, "end": v(-11.31, -15.57) * mm});
            skLineSegment(sketch, "E38.91.0", {"start": v(-10.74, -15.99) * mm, "end": v(-11, -16.4) * mm});
            skLineSegment(sketch, "E38.91.1", {"start": v(-10.31, -16.25) * mm, "end": v(-10.74, -15.99) * mm});
            skLineSegment(sketch, "E38.91.2", {"start": v(-10.58, -16.68) * mm, "end": v(-10.31, -16.25) * mm});
            skLineSegment(sketch, "E38.92.0", {"start": v(-9.71, -16.63) * mm, "end": v(-9.95, -17.06) * mm});
            skLineSegment(sketch, "E38.92.1", {"start": v(-9.27, -16.87) * mm, "end": v(-9.71, -16.63) * mm});
            skLineSegment(sketch, "E38.92.2", {"start": v(-9.51, -17.3) * mm, "end": v(-9.27, -16.87) * mm});
            skLineSegment(sketch, "E38.93.0", {"start": v(-8.65, -17.2) * mm, "end": v(-8.86, -17.65) * mm});
            skLineSegment(sketch, "E38.93.1", {"start": v(-8.2, -17.42) * mm, "end": v(-8.65, -17.2) * mm});
            skLineSegment(sketch, "E38.93.2", {"start": v(-8.4, -17.87) * mm, "end": v(-8.2, -17.42) * mm});
            skLineSegment(sketch, "E38.94.0", {"start": v(-7.55, -17.71) * mm, "end": v(-7.73, -18.17) * mm});
            skLineSegment(sketch, "E38.94.1", {"start": v(-7.09, -17.9) * mm, "end": v(-7.55, -17.71) * mm});
            skLineSegment(sketch, "E38.94.2", {"start": v(-7.27, -18.36) * mm, "end": v(-7.09, -17.9) * mm});
            skLineSegment(sketch, "E38.95.0", {"start": v(-6.42, -18.15) * mm, "end": v(-6.58, -18.62) * mm});
            skLineSegment(sketch, "E38.95.1", {"start": v(-5.95, -18.3) * mm, "end": v(-6.42, -18.15) * mm});
            skLineSegment(sketch, "E38.95.2", {"start": v(-6.1, -18.78) * mm, "end": v(-5.95, -18.3) * mm});
            skLineSegment(sketch, "E38.96.0", {"start": v(-5.27, -18.52) * mm, "end": v(-5.4, -19) * mm});
            skLineSegment(sketch, "E38.96.1", {"start": v(-4.79, -18.65) * mm, "end": v(-5.27, -18.52) * mm});
            skLineSegment(sketch, "E38.96.2", {"start": v(-4.91, -19.13) * mm, "end": v(-4.79, -18.65) * mm});
            skLineSegment(sketch, "E38.97.0", {"start": v(-4.1, -18.82) * mm, "end": v(-4.2, -19.3) * mm});
            skLineSegment(sketch, "E38.97.1", {"start": v(-3.6, -18.9) * mm, "end": v(-4.1, -18.82) * mm});
            skLineSegment(sketch, "E38.97.2", {"start": v(-3.7, -19.4) * mm, "end": v(-3.6, -18.9) * mm});
            skLineSegment(sketch, "E38.98.0", {"start": v(-2.9, -19.04) * mm, "end": v(-2.97, -19.53) * mm});
            skLineSegment(sketch, "E38.98.1", {"start": v(-2.41, -19.1) * mm, "end": v(-2.9, -19.04) * mm});
            skLineSegment(sketch, "E38.98.2", {"start": v(-2.48, -19.6) * mm, "end": v(-2.41, -19.1) * mm});
            skLineSegment(sketch, "E38.99.0", {"start": v(-1.7, -19.18) * mm, "end": v(-1.74, -19.67) * mm});
            skLineSegment(sketch, "E38.99.1", {"start": v(-1.2, -19.21) * mm, "end": v(-1.7, -19.18) * mm});
            skLineSegment(sketch, "E38.99.2", {"start": v(-1.24, -19.71) * mm, "end": v(-1.2, -19.21) * mm});
            skCircle(sketch, "E39.0", {"center": v(0, 0) * mm, "radius": 10.5 * mm});
            skSolve(sketch);
        }
        {
            var Q0;
            Q0=makeQuery(id+"F1.opRevolve","SWEPT_EDGE",EDGE,{"disambiguationData":[OSD([sQuery(id+"F0.wireOp",EDGE,"E1"),sQuery(id+"F0.wireOp",EDGE,"E2")])]});
            var Q1;
            Q1=makeQuery(id+"F1.opRevolve","SWEPT_EDGE",EDGE,{"disambiguationData":[OSD([sQuery(id+"F0.wireOp",EDGE,"E4"),sQuery(id+"F0.wireOp",EDGE,"E5")])]});
            var Q2;
            Q2=makeQuery(id+"F1.opRevolve","SWEPT_EDGE",EDGE,{"disambiguationData":[OSD([sQuery(id+"F0.wireOp",EDGE,"E1"),sQuery(id+"F0.wireOp",EDGE,"E22")])]});
            var Q3;
            Q3=makeQuery(id+"F1.opRevolve","SWEPT_EDGE",EDGE,{"disambiguationData":[OSD([sQuery(id+"F0.wireOp",EDGE,"E19"),sQuery(id+"F0.wireOp",EDGE,"E20")])]});
            chamfer(context, id + "F3", {"entities" : qUnion([Q0, Q1, Q2, Q3]), "width" : 1 * mm, "tangentPropagation" : true});
        }
        {
            var Q0;
            {var subQ0=sQuery(id+"F2.wireOp",EDGE,"E25");Q0=makeQuery(id+"F2.imprint","IMPRINT",FACE,{"disambiguationData":[TD([[makeQuery(id+"F2.imprint","IMPRINT",EDGE,{"derivedFrom":subQ0}),1.0]])]});}
            var Q1;
            {var subQ0=sQuery(id+"F2.wireOp",EDGE,"E34.1.0");Q1=makeQuery(id+"F2.imprint","IMPRINT",FACE,{"disambiguationData":[TD([[makeQuery(id+"F2.imprint","IMPRINT",EDGE,{"derivedFrom":subQ0}),1.0]])]});}
            var Q2;
            {var subQ1=sQuery(id+"F2.wireOp",EDGE,"E31.MirrorCS");Q2=makeQuery(id+"F2.imprint","IMPRINT",FACE,{"disambiguationData":[TD([[makeQuery(id+"F2.imprint","IMPRINT",EDGE,{"derivedFrom":subQ1}),-1.0]])]});}
            var Q3;
            Q3=makeQuery(id+"F2.imprint","IMPRINT",FACE,{"disambiguationData":[TD([[makeQuery(id+"F2.imprint","IMPRINT",EDGE,{"derivedFrom":sQuery(id+"F2.wireOp",EDGE,"E34.1.3")}),-1.0]])]});
            extrude(context, id + "F4", {"entities" : qUnion([Q0, Q1, Q2, Q3]), "operationType" : NewBodyOperationType.ADD, "oppositeDirection" : true, "depth" : 25 * mm, "hasSecondDirection" : true, "secondDirectionOppositeDirection" : true, "secondDirectionDepth" : 3.5 * mm});
        }
        {
            var Q0;
            {var subQ1=sQuery(id+"F2.wireOp",EDGE,"E38.115.0");Q0=makeQuery(id+"F2.imprint","IMPRINT",FACE,{"disambiguationData":[TD([[makeQuery(id+"F2.imprint","IMPRINT",EDGE,{"derivedFrom":subQ1}),1.0]])]});}
            var Q1;
            {var subQ1=sQuery(id+"F2.wireOp",EDGE,"E38.113.0");Q1=makeQuery(id+"F2.imprint","IMPRINT",FACE,{"disambiguationData":[TD([[makeQuery(id+"F2.imprint","IMPRINT",EDGE,{"derivedFrom":subQ1}),1.0]])]});}
            var Q2;
            {var subQ1=sQuery(id+"F2.wireOp",EDGE,"E38.117.0");Q2=makeQuery(id+"F2.imprint","IMPRINT",FACE,{"disambiguationData":[TD([[makeQuery(id+"F2.imprint","IMPRINT",EDGE,{"derivedFrom":subQ1}),1.0]])]});}
            var Q3;
            {var subQ1=sQuery(id+"F2.wireOp",EDGE,"E38.53.0");Q3=makeQuery(id+"F2.imprint","IMPRINT",FACE,{"disambiguationData":[TD([[makeQuery(id+"F2.imprint","IMPRINT",EDGE,{"derivedFrom":subQ1}),1.0]])]});}
            var Q4;
            {var subQ1=sQuery(id+"F2.wireOp",EDGE,"E38.85.0");Q4=makeQuery(id+"F2.imprint","IMPRINT",FACE,{"disambiguationData":[TD([[makeQuery(id+"F2.imprint","IMPRINT",EDGE,{"derivedFrom":subQ1}),1.0]])]});}
            var Q5;
            {var subQ1=sQuery(id+"F2.wireOp",EDGE,"E38.118.0");Q5=makeQuery(id+"F2.imprint","IMPRINT",FACE,{"disambiguationData":[TD([[makeQuery(id+"F2.imprint","IMPRINT",EDGE,{"derivedFrom":subQ1}),1.0]])]});}
            var Q6;
            {var subQ1=sQuery(id+"F2.wireOp",EDGE,"E38.120.0");Q6=makeQuery(id+"F2.imprint","IMPRINT",FACE,{"disambiguationData":[TD([[makeQuery(id+"F2.imprint","IMPRINT",EDGE,{"derivedFrom":subQ1}),1.0]])]});}
            var Q7;
            {var subQ1=sQuery(id+"F2.wireOp",EDGE,"E38.88.0");Q7=makeQuery(id+"F2.imprint","IMPRINT",FACE,{"disambiguationData":[TD([[makeQuery(id+"F2.imprint","IMPRINT",EDGE,{"derivedFrom":subQ1}),1.0]])]});}
            var Q8;
            {var subQ1=sQuery(id+"F2.wireOp",EDGE,"E38.121.0");Q8=makeQuery(id+"F2.imprint","IMPRINT",FACE,{"disambiguationData":[TD([[makeQuery(id+"F2.imprint","IMPRINT",EDGE,{"derivedFrom":subQ1}),1.0]])]});}
            var Q9;
            {var subQ1=sQuery(id+"F2.wireOp",EDGE,"E38.89.0");Q9=makeQuery(id+"F2.imprint","IMPRINT",FACE,{"disambiguationData":[TD([[makeQuery(id+"F2.imprint","IMPRINT",EDGE,{"derivedFrom":subQ1}),1.0]])]});}
            var Q10;
            {var subQ0=sQuery(id+"F2.wireOp",EDGE,"E38.122.0");Q10=makeQuery(id+"F2.imprint","IMPRINT",FACE,{"disambiguationData":[TD([[makeQuery(id+"F2.imprint","IMPRINT",EDGE,{"derivedFrom":subQ0}),1.0]])]});}
            var Q11;
            {var subQ1=sQuery(id+"F2.wireOp",EDGE,"E38.15.0");Q11=makeQuery(id+"F2.imprint","IMPRINT",FACE,{"disambiguationData":[TD([[makeQuery(id+"F2.imprint","IMPRINT",EDGE,{"derivedFrom":subQ1}),1.0]])]});}
            var Q12;
            {var subQ1=sQuery(id+"F2.wireOp",EDGE,"E38.18.0");Q12=makeQuery(id+"F2.imprint","IMPRINT",FACE,{"disambiguationData":[TD([[makeQuery(id+"F2.imprint","IMPRINT",EDGE,{"derivedFrom":subQ1}),1.0]])]});}
            var Q13;
            {var subQ1=sQuery(id+"F2.wireOp",EDGE,"E38.111.0");Q13=makeQuery(id+"F2.imprint","IMPRINT",FACE,{"disambiguationData":[TD([[makeQuery(id+"F2.imprint","IMPRINT",EDGE,{"derivedFrom":subQ1}),1.0]])]});}
            var Q14;
            {var subQ1=sQuery(id+"F2.wireOp",EDGE,"E38.19.0");Q14=makeQuery(id+"F2.imprint","IMPRINT",FACE,{"disambiguationData":[TD([[makeQuery(id+"F2.imprint","IMPRINT",EDGE,{"derivedFrom":subQ1}),1.0]])]});}
            var Q15;
            {var subQ1=sQuery(id+"F2.wireOp",EDGE,"E38.127.0");Q15=makeQuery(id+"F2.imprint","IMPRINT",FACE,{"disambiguationData":[TD([[makeQuery(id+"F2.imprint","IMPRINT",EDGE,{"derivedFrom":subQ1}),1.0]])]});}
            var Q16;
            {var subQ1=sQuery(id+"F2.wireOp",EDGE,"E38.112.0");Q16=makeQuery(id+"F2.imprint","IMPRINT",FACE,{"disambiguationData":[TD([[makeQuery(id+"F2.imprint","IMPRINT",EDGE,{"derivedFrom":subQ1}),1.0]])]});}
            var Q17;
            {var subQ0=sQuery(id+"F2.wireOp",EDGE,"E38.128.0");Q17=makeQuery(id+"F2.imprint","IMPRINT",FACE,{"disambiguationData":[TD([[makeQuery(id+"F2.imprint","IMPRINT",EDGE,{"derivedFrom":subQ0}),1.0]])]});}
            var Q18;
            {var subQ1=sQuery(id+"F2.wireOp",EDGE,"E38.50.0");Q18=makeQuery(id+"F2.imprint","IMPRINT",FACE,{"disambiguationData":[TD([[makeQuery(id+"F2.imprint","IMPRINT",EDGE,{"derivedFrom":subQ1}),1.0]])]});}
            var Q19;
            {var subQ1=sQuery(id+"F2.wireOp",EDGE,"E38.42.0");Q19=makeQuery(id+"F2.imprint","IMPRINT",FACE,{"disambiguationData":[TD([[makeQuery(id+"F2.imprint","IMPRINT",EDGE,{"derivedFrom":subQ1}),1.0]])]});}
            var Q20;
            {var subQ1=sQuery(id+"F2.wireOp",EDGE,"E38.43.0");Q20=makeQuery(id+"F2.imprint","IMPRINT",FACE,{"disambiguationData":[TD([[makeQuery(id+"F2.imprint","IMPRINT",EDGE,{"derivedFrom":subQ1}),1.0]])]});}
            var Q21;
            {var subQ1=sQuery(id+"F2.wireOp",EDGE,"E38.45.0");Q21=makeQuery(id+"F2.imprint","IMPRINT",FACE,{"disambiguationData":[TD([[makeQuery(id+"F2.imprint","IMPRINT",EDGE,{"derivedFrom":subQ1}),1.0]])]});}
            var Q22;
            {var subQ1=sQuery(id+"F2.wireOp",EDGE,"E38.46.0");Q22=makeQuery(id+"F2.imprint","IMPRINT",FACE,{"disambiguationData":[TD([[makeQuery(id+"F2.imprint","IMPRINT",EDGE,{"derivedFrom":subQ1}),1.0]])]});}
            var Q23;
            {var subQ1=sQuery(id+"F2.wireOp",EDGE,"E38.52.0");Q23=makeQuery(id+"F2.imprint","IMPRINT",FACE,{"disambiguationData":[TD([[makeQuery(id+"F2.imprint","IMPRINT",EDGE,{"derivedFrom":subQ1}),1.0]])]});}
            var Q24;
            {var subQ1=sQuery(id+"F2.wireOp",EDGE,"E38.116.0");Q24=makeQuery(id+"F2.imprint","IMPRINT",FACE,{"disambiguationData":[TD([[makeQuery(id+"F2.imprint","IMPRINT",EDGE,{"derivedFrom":subQ1}),1.0]])]});}
            var Q25;
            {var subQ0=sQuery(id+"F2.wireOp",EDGE,"E38.54.0");Q25=makeQuery(id+"F2.imprint","IMPRINT",FACE,{"disambiguationData":[TD([[makeQuery(id+"F2.imprint","IMPRINT",EDGE,{"derivedFrom":subQ0}),1.0]])]});}
            var Q26;
            {var subQ0=sQuery(id+"F2.wireOp",EDGE,"E38.86.0");Q26=makeQuery(id+"F2.imprint","IMPRINT",FACE,{"disambiguationData":[TD([[makeQuery(id+"F2.imprint","IMPRINT",EDGE,{"derivedFrom":subQ0}),1.0]])]});}
            var Q27;
            {var subQ1=sQuery(id+"F2.wireOp",EDGE,"E38.87.0");Q27=makeQuery(id+"F2.imprint","IMPRINT",FACE,{"disambiguationData":[TD([[makeQuery(id+"F2.imprint","IMPRINT",EDGE,{"derivedFrom":subQ1}),1.0]])]});}
            var Q28;
            {var subQ1=sQuery(id+"F2.wireOp",EDGE,"E38.11.0");Q28=makeQuery(id+"F2.imprint","IMPRINT",FACE,{"disambiguationData":[TD([[makeQuery(id+"F2.imprint","IMPRINT",EDGE,{"derivedFrom":subQ1}),1.0]])]});}
            var Q29;
            {var subQ1=sQuery(id+"F2.wireOp",EDGE,"E38.12.0");Q29=makeQuery(id+"F2.imprint","IMPRINT",FACE,{"disambiguationData":[TD([[makeQuery(id+"F2.imprint","IMPRINT",EDGE,{"derivedFrom":subQ1}),1.0]])]});}
            var Q30;
            {var subQ1=sQuery(id+"F2.wireOp",EDGE,"E38.29.0");Q30=makeQuery(id+"F2.imprint","IMPRINT",FACE,{"disambiguationData":[TD([[makeQuery(id+"F2.imprint","IMPRINT",EDGE,{"derivedFrom":subQ1}),1.0]])]});}
            var Q31;
            {var subQ1=sQuery(id+"F2.wireOp",EDGE,"E38.13.0");Q31=makeQuery(id+"F2.imprint","IMPRINT",FACE,{"disambiguationData":[TD([[makeQuery(id+"F2.imprint","IMPRINT",EDGE,{"derivedFrom":subQ1}),1.0]])]});}
            var Q32;
            {var subQ1=sQuery(id+"F2.wireOp",EDGE,"E38.14.0");Q32=makeQuery(id+"F2.imprint","IMPRINT",FACE,{"disambiguationData":[TD([[makeQuery(id+"F2.imprint","IMPRINT",EDGE,{"derivedFrom":subQ1}),1.0]])]});}
            var Q33;
            {var subQ1=sQuery(id+"F2.wireOp",EDGE,"E38.123.0");Q33=makeQuery(id+"F2.imprint","IMPRINT",FACE,{"disambiguationData":[TD([[makeQuery(id+"F2.imprint","IMPRINT",EDGE,{"derivedFrom":subQ1}),1.0]])]});}
            var Q34;
            {var subQ1=sQuery(id+"F2.wireOp",EDGE,"E38.75.0");Q34=makeQuery(id+"F2.imprint","IMPRINT",FACE,{"disambiguationData":[TD([[makeQuery(id+"F2.imprint","IMPRINT",EDGE,{"derivedFrom":subQ1}),1.0]])]});}
            var Q35;
            {var subQ1=sQuery(id+"F2.wireOp",EDGE,"E38.125.0");Q35=makeQuery(id+"F2.imprint","IMPRINT",FACE,{"disambiguationData":[TD([[makeQuery(id+"F2.imprint","IMPRINT",EDGE,{"derivedFrom":subQ1}),1.0]])]});}
            var Q36;
            {var subQ1=sQuery(id+"F2.wireOp",EDGE,"E38.62.0");Q36=makeQuery(id+"F2.imprint","IMPRINT",FACE,{"disambiguationData":[TD([[makeQuery(id+"F2.imprint","IMPRINT",EDGE,{"derivedFrom":subQ1}),1.0]])]});}
            var Q37;
            {var subQ1=sQuery(id+"F2.wireOp",EDGE,"E38.126.0");Q37=makeQuery(id+"F2.imprint","IMPRINT",FACE,{"disambiguationData":[TD([[makeQuery(id+"F2.imprint","IMPRINT",EDGE,{"derivedFrom":subQ1}),1.0]])]});}
            var Q38;
            {var subQ1=sQuery(id+"F2.wireOp",EDGE,"E38.95.0");Q38=makeQuery(id+"F2.imprint","IMPRINT",FACE,{"disambiguationData":[TD([[makeQuery(id+"F2.imprint","IMPRINT",EDGE,{"derivedFrom":subQ1}),1.0]])]});}
            var Q39;
            {var subQ1=sQuery(id+"F2.wireOp",EDGE,"E38.51.0");Q39=makeQuery(id+"F2.imprint","IMPRINT",FACE,{"disambiguationData":[TD([[makeQuery(id+"F2.imprint","IMPRINT",EDGE,{"derivedFrom":subQ1}),1.0]])]});}
            var Q40;
            {var subQ1=sQuery(id+"F2.wireOp",EDGE,"E38.44.0");Q40=makeQuery(id+"F2.imprint","IMPRINT",FACE,{"disambiguationData":[TD([[makeQuery(id+"F2.imprint","IMPRINT",EDGE,{"derivedFrom":subQ1}),1.0]])]});}
            var Q41;
            {var subQ0=sQuery(id+"F2.wireOp",EDGE,"E38.99.0");Q41=makeQuery(id+"F2.imprint","IMPRINT",FACE,{"disambiguationData":[TD([[makeQuery(id+"F2.imprint","IMPRINT",EDGE,{"derivedFrom":subQ0}),1.0]])]});}
            var Q42;
            {var subQ1=sQuery(id+"F2.wireOp",EDGE,"E38.97.0");Q42=makeQuery(id+"F2.imprint","IMPRINT",FACE,{"disambiguationData":[TD([[makeQuery(id+"F2.imprint","IMPRINT",EDGE,{"derivedFrom":subQ1}),1.0]])]});}
            var Q43;
            {var subQ1=sQuery(id+"F2.wireOp",EDGE,"E38.21.0");Q43=makeQuery(id+"F2.imprint","IMPRINT",FACE,{"disambiguationData":[TD([[makeQuery(id+"F2.imprint","IMPRINT",EDGE,{"derivedFrom":subQ1}),1.0]])]});}
            var Q44;
            {var subQ1=sQuery(id+"F2.wireOp",EDGE,"E38.100.0");Q44=makeQuery(id+"F2.imprint","IMPRINT",FACE,{"disambiguationData":[TD([[makeQuery(id+"F2.imprint","IMPRINT",EDGE,{"derivedFrom":subQ1}),1.0]])]});}
            var Q45;
            {var subQ1=sQuery(id+"F2.wireOp",EDGE,"E38.84.0");Q45=makeQuery(id+"F2.imprint","IMPRINT",FACE,{"disambiguationData":[TD([[makeQuery(id+"F2.imprint","IMPRINT",EDGE,{"derivedFrom":subQ1}),1.0]])]});}
            var Q46;
            {var subQ1=sQuery(id+"F2.wireOp",EDGE,"E38.24.0");Q46=makeQuery(id+"F2.imprint","IMPRINT",FACE,{"disambiguationData":[TD([[makeQuery(id+"F2.imprint","IMPRINT",EDGE,{"derivedFrom":subQ1}),1.0]])]});}
            var Q47;
            {var subQ1=sQuery(id+"F2.wireOp",EDGE,"E38.9.0");Q47=makeQuery(id+"F2.imprint","IMPRINT",FACE,{"disambiguationData":[TD([[makeQuery(id+"F2.imprint","IMPRINT",EDGE,{"derivedFrom":subQ1}),1.0]])]});}
            var Q48;
            {var subQ1=sQuery(id+"F2.wireOp",EDGE,"E38.26.0");Q48=makeQuery(id+"F2.imprint","IMPRINT",FACE,{"disambiguationData":[TD([[makeQuery(id+"F2.imprint","IMPRINT",EDGE,{"derivedFrom":subQ1}),1.0]])]});}
            var Q49;
            {var subQ1=sQuery(id+"F2.wireOp",EDGE,"E38.55.0");Q49=makeQuery(id+"F2.imprint","IMPRINT",FACE,{"disambiguationData":[TD([[makeQuery(id+"F2.imprint","IMPRINT",EDGE,{"derivedFrom":subQ1}),1.0]])]});}
            var Q50;
            {var subQ1=sQuery(id+"F2.wireOp",EDGE,"E38.119.0");Q50=makeQuery(id+"F2.imprint","IMPRINT",FACE,{"disambiguationData":[TD([[makeQuery(id+"F2.imprint","IMPRINT",EDGE,{"derivedFrom":subQ1}),1.0]])]});}
            var Q51;
            {var subQ1=sQuery(id+"F2.wireOp",EDGE,"E38.57.0");Q51=makeQuery(id+"F2.imprint","IMPRINT",FACE,{"disambiguationData":[TD([[makeQuery(id+"F2.imprint","IMPRINT",EDGE,{"derivedFrom":subQ1}),1.0]])]});}
            var Q52;
            {var subQ1=sQuery(id+"F2.wireOp",EDGE,"E38.90.0");Q52=makeQuery(id+"F2.imprint","IMPRINT",FACE,{"disambiguationData":[TD([[makeQuery(id+"F2.imprint","IMPRINT",EDGE,{"derivedFrom":subQ1}),1.0]])]});}
            var Q53;
            {var subQ0=sQuery(id+"F2.wireOp",EDGE,"E38.30.0");Q53=makeQuery(id+"F2.imprint","IMPRINT",FACE,{"disambiguationData":[TD([[makeQuery(id+"F2.imprint","IMPRINT",EDGE,{"derivedFrom":subQ0}),1.0]])]});}
            var Q54;
            {var subQ1=sQuery(id+"F2.wireOp",EDGE,"E38.59.0");Q54=makeQuery(id+"F2.imprint","IMPRINT",FACE,{"disambiguationData":[TD([[makeQuery(id+"F2.imprint","IMPRINT",EDGE,{"derivedFrom":subQ1}),1.0]])]});}
            var Q55;
            {var subQ1=sQuery(id+"F2.wireOp",EDGE,"E38.124.0");Q55=makeQuery(id+"F2.imprint","IMPRINT",FACE,{"disambiguationData":[TD([[makeQuery(id+"F2.imprint","IMPRINT",EDGE,{"derivedFrom":subQ1}),1.0]])]});}
            var Q56;
            {var subQ1=sQuery(id+"F2.wireOp",EDGE,"E38.17.0");Q56=makeQuery(id+"F2.imprint","IMPRINT",FACE,{"disambiguationData":[TD([[makeQuery(id+"F2.imprint","IMPRINT",EDGE,{"derivedFrom":subQ1}),1.0]])]});}
            var Q57;
            {var subQ0=sQuery(id+"F2.wireOp",EDGE,"E38.78.0");Q57=makeQuery(id+"F2.imprint","IMPRINT",FACE,{"disambiguationData":[TD([[makeQuery(id+"F2.imprint","IMPRINT",EDGE,{"derivedFrom":subQ0}),1.0]])]});}
            var Q58;
            {var subQ1=sQuery(id+"F2.wireOp",EDGE,"E38.79.0");Q58=makeQuery(id+"F2.imprint","IMPRINT",FACE,{"disambiguationData":[TD([[makeQuery(id+"F2.imprint","IMPRINT",EDGE,{"derivedFrom":subQ1}),1.0]])]});}
            var Q59;
            {var subQ0=sQuery(id+"F2.wireOp",EDGE,"E38.63.0");Q59=makeQuery(id+"F2.imprint","IMPRINT",FACE,{"disambiguationData":[TD([[makeQuery(id+"F2.imprint","IMPRINT",EDGE,{"derivedFrom":subQ0}),1.0]])]});}
            var Q60;
            {var subQ1=sQuery(id+"F2.wireOp",EDGE,"E38.3.0");Q60=makeQuery(id+"F2.imprint","IMPRINT",FACE,{"disambiguationData":[TD([[makeQuery(id+"F2.imprint","IMPRINT",EDGE,{"derivedFrom":subQ1}),1.0]])]});}
            var Q61;
            {var subQ1=sQuery(id+"F2.wireOp",EDGE,"E38.96.0");Q61=makeQuery(id+"F2.imprint","IMPRINT",FACE,{"disambiguationData":[TD([[makeQuery(id+"F2.imprint","IMPRINT",EDGE,{"derivedFrom":subQ1}),1.0]])]});}
            var Q62;
            {var subQ1=sQuery(id+"F2.wireOp",EDGE,"E38.49.0");Q62=makeQuery(id+"F2.imprint","IMPRINT",FACE,{"disambiguationData":[TD([[makeQuery(id+"F2.imprint","IMPRINT",EDGE,{"derivedFrom":subQ1}),1.0]])]});}
            var Q63;
            {var subQ1=sQuery(id+"F2.wireOp",EDGE,"E38.38.0");Q63=makeQuery(id+"F2.imprint","IMPRINT",FACE,{"disambiguationData":[TD([[makeQuery(id+"F2.imprint","IMPRINT",EDGE,{"derivedFrom":subQ1}),1.0]])]});}
            var Q64;
            {var subQ1=sQuery(id+"F2.wireOp",EDGE,"E38.131.0");Q64=makeQuery(id+"F2.imprint","IMPRINT",FACE,{"disambiguationData":[TD([[makeQuery(id+"F2.imprint","IMPRINT",EDGE,{"derivedFrom":subQ1}),1.0]])]});}
            var Q65;
            {var subQ1=sQuery(id+"F2.wireOp",EDGE,"E38.23.0");Q65=makeQuery(id+"F2.imprint","IMPRINT",FACE,{"disambiguationData":[TD([[makeQuery(id+"F2.imprint","IMPRINT",EDGE,{"derivedFrom":subQ1}),1.0]])]});}
            var Q66;
            {var subQ1=sQuery(id+"F2.wireOp",EDGE,"E38.5.0");Q66=makeQuery(id+"F2.imprint","IMPRINT",FACE,{"disambiguationData":[TD([[makeQuery(id+"F2.imprint","IMPRINT",EDGE,{"derivedFrom":subQ1}),1.0]])]});}
            var Q67;
            {var subQ1=sQuery(id+"F2.wireOp",EDGE,"E38.98.0");Q67=makeQuery(id+"F2.imprint","IMPRINT",FACE,{"disambiguationData":[TD([[makeQuery(id+"F2.imprint","IMPRINT",EDGE,{"derivedFrom":subQ1}),1.0]])]});}
            var Q68;
            {var subQ1=sQuery(id+"F2.wireOp",EDGE,"E38.133.0");Q68=makeQuery(id+"F2.imprint","IMPRINT",FACE,{"disambiguationData":[TD([[makeQuery(id+"F2.imprint","IMPRINT",EDGE,{"derivedFrom":subQ1}),1.0]])]});}
            var Q69;
            {var subQ1=sQuery(id+"F2.wireOp",EDGE,"E38.101.0");Q69=makeQuery(id+"F2.imprint","IMPRINT",FACE,{"disambiguationData":[TD([[makeQuery(id+"F2.imprint","IMPRINT",EDGE,{"derivedFrom":subQ1}),1.0]])]});}
            var Q70;
            {var subQ1=sQuery(id+"F2.wireOp",EDGE,"E38.56.0");Q70=makeQuery(id+"F2.imprint","IMPRINT",FACE,{"disambiguationData":[TD([[makeQuery(id+"F2.imprint","IMPRINT",EDGE,{"derivedFrom":subQ1}),1.0]])]});}
            var Q71;
            {var subQ1=sQuery(id+"F2.wireOp",EDGE,"E38.28.0");Q71=makeQuery(id+"F2.imprint","IMPRINT",FACE,{"disambiguationData":[TD([[makeQuery(id+"F2.imprint","IMPRINT",EDGE,{"derivedFrom":subQ1}),1.0]])]});}
            var Q72;
            {var subQ1=sQuery(id+"F2.wireOp",EDGE,"E38.58.0");Q72=makeQuery(id+"F2.imprint","IMPRINT",FACE,{"disambiguationData":[TD([[makeQuery(id+"F2.imprint","IMPRINT",EDGE,{"derivedFrom":subQ1}),1.0]])]});}
            var Q73;
            {var subQ1=sQuery(id+"F2.wireOp",EDGE,"E38.76.0");Q73=makeQuery(id+"F2.imprint","IMPRINT",FACE,{"disambiguationData":[TD([[makeQuery(id+"F2.imprint","IMPRINT",EDGE,{"derivedFrom":subQ1}),1.0]])]});}
            var Q74;
            {var subQ1=sQuery(id+"F2.wireOp",EDGE,"E38.60.0");Q74=makeQuery(id+"F2.imprint","IMPRINT",FACE,{"disambiguationData":[TD([[makeQuery(id+"F2.imprint","IMPRINT",EDGE,{"derivedFrom":subQ1}),1.0]])]});}
            var Q75;
            {var subQ1=sQuery(id+"F2.wireOp",EDGE,"E38.109.0");Q75=makeQuery(id+"F2.imprint","IMPRINT",FACE,{"disambiguationData":[TD([[makeQuery(id+"F2.imprint","IMPRINT",EDGE,{"derivedFrom":subQ1}),1.0]])]});}
            var Q76;
            {var subQ1=sQuery(id+"F2.wireOp",EDGE,"E38.80.0");Q76=makeQuery(id+"F2.imprint","IMPRINT",FACE,{"disambiguationData":[TD([[makeQuery(id+"F2.imprint","IMPRINT",EDGE,{"derivedFrom":subQ1}),1.0]])]});}
            var Q77;
            {var subQ1=sQuery(id+"F2.wireOp",EDGE,"E38.40.0");Q77=makeQuery(id+"F2.imprint","IMPRINT",FACE,{"disambiguationData":[TD([[makeQuery(id+"F2.imprint","IMPRINT",EDGE,{"derivedFrom":subQ1}),1.0]])]});}
            var Q78;
            {var subQ1=sQuery(id+"F2.wireOp",EDGE,"E38.47.0");Q78=makeQuery(id+"F2.imprint","IMPRINT",FACE,{"disambiguationData":[TD([[makeQuery(id+"F2.imprint","IMPRINT",EDGE,{"derivedFrom":subQ1}),1.0]])]});}
            var Q79;
            {var subQ1=sQuery(id+"F2.wireOp",EDGE,"E38.130.0");Q79=makeQuery(id+"F2.imprint","IMPRINT",FACE,{"disambiguationData":[TD([[makeQuery(id+"F2.imprint","IMPRINT",EDGE,{"derivedFrom":subQ1}),1.0]])]});}
            var Q80;
            {var subQ1=sQuery(id+"F2.wireOp",EDGE,"E38.8.0");Q80=makeQuery(id+"F2.imprint","IMPRINT",FACE,{"disambiguationData":[TD([[makeQuery(id+"F2.imprint","IMPRINT",EDGE,{"derivedFrom":subQ1}),1.0]])]});}
            var Q81;
            {var subQ1=sQuery(id+"F2.wireOp",EDGE,"E38.25.0");Q81=makeQuery(id+"F2.imprint","IMPRINT",FACE,{"disambiguationData":[TD([[makeQuery(id+"F2.imprint","IMPRINT",EDGE,{"derivedFrom":subQ1}),1.0]])]});}
            var Q82;
            {var subQ1=sQuery(id+"F2.wireOp",EDGE,"E38.27.0");Q82=makeQuery(id+"F2.imprint","IMPRINT",FACE,{"disambiguationData":[TD([[makeQuery(id+"F2.imprint","IMPRINT",EDGE,{"derivedFrom":subQ1}),1.0]])]});}
            var Q83;
            {var subQ1=sQuery(id+"F2.wireOp",EDGE,"E38.108.0");Q83=makeQuery(id+"F2.imprint","IMPRINT",FACE,{"disambiguationData":[TD([[makeQuery(id+"F2.imprint","IMPRINT",EDGE,{"derivedFrom":subQ1}),1.0]])]});}
            var Q84;
            {var subQ0=sQuery(id+"F2.wireOp",EDGE,"E38.110.0");Q84=makeQuery(id+"F2.imprint","IMPRINT",FACE,{"disambiguationData":[TD([[makeQuery(id+"F2.imprint","IMPRINT",EDGE,{"derivedFrom":subQ0}),1.0]])]});}
            var Q85;
            {var subQ1=sQuery(id+"F2.wireOp",EDGE,"E38.35.0");Q85=makeQuery(id+"F2.imprint","IMPRINT",FACE,{"disambiguationData":[TD([[makeQuery(id+"F2.imprint","IMPRINT",EDGE,{"derivedFrom":subQ1}),1.0]])]});}
            var Q86;
            {var subQ1=sQuery(id+"F2.wireOp",EDGE,"E38.37.0");Q86=makeQuery(id+"F2.imprint","IMPRINT",FACE,{"disambiguationData":[TD([[makeQuery(id+"F2.imprint","IMPRINT",EDGE,{"derivedFrom":subQ1}),1.0]])]});}
            var Q87;
            {var subQ1=sQuery(id+"F2.wireOp",EDGE,"E38.39.0");Q87=makeQuery(id+"F2.imprint","IMPRINT",FACE,{"disambiguationData":[TD([[makeQuery(id+"F2.imprint","IMPRINT",EDGE,{"derivedFrom":subQ1}),1.0]])]});}
            var Q88;
            {var subQ1=sQuery(id+"F2.wireOp",EDGE,"E38.41.0");Q88=makeQuery(id+"F2.imprint","IMPRINT",FACE,{"disambiguationData":[TD([[makeQuery(id+"F2.imprint","IMPRINT",EDGE,{"derivedFrom":subQ1}),1.0]])]});}
            var Q89;
            {var subQ1=sQuery(id+"F2.wireOp",EDGE,"E38.103.0");Q89=makeQuery(id+"F2.imprint","IMPRINT",FACE,{"disambiguationData":[TD([[makeQuery(id+"F2.imprint","IMPRINT",EDGE,{"derivedFrom":subQ1}),1.0]])]});}
            var Q90;
            {var subQ1=sQuery(id+"F2.wireOp",EDGE,"E38.106.0");Q90=makeQuery(id+"F2.imprint","IMPRINT",FACE,{"disambiguationData":[TD([[makeQuery(id+"F2.imprint","IMPRINT",EDGE,{"derivedFrom":subQ1}),1.0]])]});}
            var Q91;
            {var subQ1=sQuery(id+"F2.wireOp",EDGE,"E38.31.0");Q91=makeQuery(id+"F2.imprint","IMPRINT",FACE,{"disambiguationData":[TD([[makeQuery(id+"F2.imprint","IMPRINT",EDGE,{"derivedFrom":subQ1}),1.0]])]});}
            var Q92;
            {var subQ1=sQuery(id+"F2.wireOp",EDGE,"E38.33.0");Q92=makeQuery(id+"F2.imprint","IMPRINT",FACE,{"disambiguationData":[TD([[makeQuery(id+"F2.imprint","IMPRINT",EDGE,{"derivedFrom":subQ1}),1.0]])]});}
            var Q93;
            {var subQ0=sQuery(id+"F2.wireOp",EDGE,"E38.94.0");Q93=makeQuery(id+"F2.imprint","IMPRINT",FACE,{"disambiguationData":[TD([[makeQuery(id+"F2.imprint","IMPRINT",EDGE,{"derivedFrom":subQ0}),1.0]])]});}
            var Q94;
            {var subQ0=sQuery(id+"F2.wireOp",EDGE,"E38.34.0");Q94=makeQuery(id+"F2.imprint","IMPRINT",FACE,{"disambiguationData":[TD([[makeQuery(id+"F2.imprint","IMPRINT",EDGE,{"derivedFrom":subQ0}),1.0]])]});}
            var Q95;
            {var subQ1=sQuery(id+"F2.wireOp",EDGE,"E38.36.0");Q95=makeQuery(id+"F2.imprint","IMPRINT",FACE,{"disambiguationData":[TD([[makeQuery(id+"F2.imprint","IMPRINT",EDGE,{"derivedFrom":subQ1}),1.0]])]});}
            var Q96;
            {var subQ1=sQuery(id+"F2.wireOp",EDGE,"E38.132.0");Q96=makeQuery(id+"F2.imprint","IMPRINT",FACE,{"disambiguationData":[TD([[makeQuery(id+"F2.imprint","IMPRINT",EDGE,{"derivedFrom":subQ1}),1.0]])]});}
            var Q97;
            {var subQ1=sQuery(id+"F2.wireOp",EDGE,"E38.102.0");Q97=makeQuery(id+"F2.imprint","IMPRINT",FACE,{"disambiguationData":[TD([[makeQuery(id+"F2.imprint","IMPRINT",EDGE,{"derivedFrom":subQ1}),1.0]])]});}
            var Q98;
            {var subQ1=sQuery(id+"F2.wireOp",EDGE,"E38.136.0");Q98=makeQuery(id+"F2.imprint","IMPRINT",FACE,{"disambiguationData":[TD([[makeQuery(id+"F2.imprint","IMPRINT",EDGE,{"derivedFrom":subQ1}),1.0]])]});}
            var Q99;
            {var subQ1=sQuery(id+"F2.wireOp",EDGE,"E38.104.0");Q99=makeQuery(id+"F2.imprint","IMPRINT",FACE,{"disambiguationData":[TD([[makeQuery(id+"F2.imprint","IMPRINT",EDGE,{"derivedFrom":subQ1}),1.0]])]});}
            var Q100;
            {var subQ1=sQuery(id+"F2.wireOp",EDGE,"E38.137.0");Q100=makeQuery(id+"F2.imprint","IMPRINT",FACE,{"disambiguationData":[TD([[makeQuery(id+"F2.imprint","IMPRINT",EDGE,{"derivedFrom":subQ1}),1.0]])]});}
            var Q101;
            {var subQ1=sQuery(id+"F2.wireOp",EDGE,"E38.105.0");Q101=makeQuery(id+"F2.imprint","IMPRINT",FACE,{"disambiguationData":[TD([[makeQuery(id+"F2.imprint","IMPRINT",EDGE,{"derivedFrom":subQ1}),1.0]])]});}
            var Q102;
            {var subQ1=sQuery(id+"F2.wireOp",EDGE,"E38.138.0");Q102=makeQuery(id+"F2.imprint","IMPRINT",FACE,{"disambiguationData":[TD([[makeQuery(id+"F2.imprint","IMPRINT",EDGE,{"derivedFrom":subQ1}),1.0]])]});}
            var Q103;
            {var subQ1=sQuery(id+"F2.wireOp",EDGE,"E38.139.0");Q103=makeQuery(id+"F2.imprint","IMPRINT",FACE,{"disambiguationData":[TD([[makeQuery(id+"F2.imprint","IMPRINT",EDGE,{"derivedFrom":subQ1}),1.0]])]});}
            var Q104;
            {var subQ1=sQuery(id+"F2.wireOp",EDGE,"E35");Q104=makeQuery(id+"F2.imprint","IMPRINT",FACE,{"disambiguationData":[TD([[makeQuery(id+"F2.imprint","IMPRINT",EDGE,{"derivedFrom":subQ1}),1.0]])]});}
            var Q105;
            {var subQ1=sQuery(id+"F2.wireOp",EDGE,"E38.65.0");Q105=makeQuery(id+"F2.imprint","IMPRINT",FACE,{"disambiguationData":[TD([[makeQuery(id+"F2.imprint","IMPRINT",EDGE,{"derivedFrom":subQ1}),1.0]])]});}
            var Q106;
            {var subQ1=sQuery(id+"F2.wireOp",EDGE,"E38.134.0");Q106=makeQuery(id+"F2.imprint","IMPRINT",FACE,{"disambiguationData":[TD([[makeQuery(id+"F2.imprint","IMPRINT",EDGE,{"derivedFrom":subQ1}),1.0]])]});}
            var Q107;
            {var subQ1=sQuery(id+"F2.wireOp",EDGE,"E38.135.0");Q107=makeQuery(id+"F2.imprint","IMPRINT",FACE,{"disambiguationData":[TD([[makeQuery(id+"F2.imprint","IMPRINT",EDGE,{"derivedFrom":subQ1}),1.0]])]});}
            var Q108;
            {var subQ1=sQuery(id+"F2.wireOp",EDGE,"E38.72.0");Q108=makeQuery(id+"F2.imprint","IMPRINT",FACE,{"disambiguationData":[TD([[makeQuery(id+"F2.imprint","IMPRINT",EDGE,{"derivedFrom":subQ1}),1.0]])]});}
            var Q109;
            {var subQ0=sQuery(id+"F2.wireOp",EDGE,"E38.74.0");Q109=makeQuery(id+"F2.imprint","IMPRINT",FACE,{"disambiguationData":[TD([[makeQuery(id+"F2.imprint","IMPRINT",EDGE,{"derivedFrom":subQ0}),1.0]])]});}
            var Q110;
            {var subQ1=sQuery(id+"F2.wireOp",EDGE,"E38.107.0");Q110=makeQuery(id+"F2.imprint","IMPRINT",FACE,{"disambiguationData":[TD([[makeQuery(id+"F2.imprint","IMPRINT",EDGE,{"derivedFrom":subQ1}),1.0]])]});}
            var Q111;
            {var subQ1=sQuery(id+"F2.wireOp",EDGE,"E38.1.0");Q111=makeQuery(id+"F2.imprint","IMPRINT",FACE,{"disambiguationData":[TD([[makeQuery(id+"F2.imprint","IMPRINT",EDGE,{"derivedFrom":subQ1}),1.0]])]});}
            var Q112;
            {var subQ1=sQuery(id+"F2.wireOp",EDGE,"E38.66.0");Q112=makeQuery(id+"F2.imprint","IMPRINT",FACE,{"disambiguationData":[TD([[makeQuery(id+"F2.imprint","IMPRINT",EDGE,{"derivedFrom":subQ1}),1.0]])]});}
            var Q113;
            {var subQ0=sQuery(id+"F2.wireOp",EDGE,"E38.70.0");Q113=makeQuery(id+"F2.imprint","IMPRINT",FACE,{"disambiguationData":[TD([[makeQuery(id+"F2.imprint","IMPRINT",EDGE,{"derivedFrom":subQ0}),1.0]])]});}
            var Q114;
            {var subQ1=sQuery(id+"F2.wireOp",EDGE,"E38.2.0");Q114=makeQuery(id+"F2.imprint","IMPRINT",FACE,{"disambiguationData":[TD([[makeQuery(id+"F2.imprint","IMPRINT",EDGE,{"derivedFrom":subQ1}),1.0]])]});}
            var Q115;
            {var subQ1=sQuery(id+"F2.wireOp",EDGE,"E38.67.0");Q115=makeQuery(id+"F2.imprint","IMPRINT",FACE,{"disambiguationData":[TD([[makeQuery(id+"F2.imprint","IMPRINT",EDGE,{"derivedFrom":subQ1}),1.0]])]});}
            var Q116;
            {var subQ0=sQuery(id+"F2.wireOp",EDGE,"E38.69.0");Q116=makeQuery(id+"F2.imprint","IMPRINT",FACE,{"disambiguationData":[TD([[makeQuery(id+"F2.imprint","IMPRINT",EDGE,{"derivedFrom":subQ0}),1.0]])]});}
            var Q117;
            {var subQ1=sQuery(id+"F2.wireOp",EDGE,"E38.71.0");Q117=makeQuery(id+"F2.imprint","IMPRINT",FACE,{"disambiguationData":[TD([[makeQuery(id+"F2.imprint","IMPRINT",EDGE,{"derivedFrom":subQ1}),1.0]])]});}
            var Q118;
            {var subQ1=sQuery(id+"F2.wireOp",EDGE,"E38.68.0");Q118=makeQuery(id+"F2.imprint","IMPRINT",FACE,{"disambiguationData":[TD([[makeQuery(id+"F2.imprint","IMPRINT",EDGE,{"derivedFrom":subQ1}),1.0]])]});}
            var Q119;
            {var subQ1=sQuery(id+"F2.wireOp",EDGE,"E38.48.0");Q119=makeQuery(id+"F2.imprint","IMPRINT",FACE,{"disambiguationData":[TD([[makeQuery(id+"F2.imprint","IMPRINT",EDGE,{"derivedFrom":subQ1}),1.0]])]});}
            var Q120;
            {var subQ1=sQuery(id+"F2.wireOp",EDGE,"E38.32.0");Q120=makeQuery(id+"F2.imprint","IMPRINT",FACE,{"disambiguationData":[TD([[makeQuery(id+"F2.imprint","IMPRINT",EDGE,{"derivedFrom":subQ1}),1.0]])]});}
            var Q121;
            {var subQ1=sQuery(id+"F2.wireOp",EDGE,"E38.22.0");Q121=makeQuery(id+"F2.imprint","IMPRINT",FACE,{"disambiguationData":[TD([[makeQuery(id+"F2.imprint","IMPRINT",EDGE,{"derivedFrom":subQ1}),1.0]])]});}
            var Q122;
            {var subQ1=sQuery(id+"F2.wireOp",EDGE,"E38.20.0");Q122=makeQuery(id+"F2.imprint","IMPRINT",FACE,{"disambiguationData":[TD([[makeQuery(id+"F2.imprint","IMPRINT",EDGE,{"derivedFrom":subQ1}),1.0]])]});}
            var Q123;
            {var subQ1=sQuery(id+"F2.wireOp",EDGE,"E38.16.0");Q123=makeQuery(id+"F2.imprint","IMPRINT",FACE,{"disambiguationData":[TD([[makeQuery(id+"F2.imprint","IMPRINT",EDGE,{"derivedFrom":subQ1}),1.0]])]});}
            var Q124;
            {var subQ1=sQuery(id+"F2.wireOp",EDGE,"E38.10.0");Q124=makeQuery(id+"F2.imprint","IMPRINT",FACE,{"disambiguationData":[TD([[makeQuery(id+"F2.imprint","IMPRINT",EDGE,{"derivedFrom":subQ1}),1.0]])]});}
            var Q125;
            {var subQ1=sQuery(id+"F2.wireOp",EDGE,"E38.7.0");Q125=makeQuery(id+"F2.imprint","IMPRINT",FACE,{"disambiguationData":[TD([[makeQuery(id+"F2.imprint","IMPRINT",EDGE,{"derivedFrom":subQ1}),1.0]])]});}
            var Q126;
            {var subQ1=sQuery(id+"F2.wireOp",EDGE,"E38.6.0");Q126=makeQuery(id+"F2.imprint","IMPRINT",FACE,{"disambiguationData":[TD([[makeQuery(id+"F2.imprint","IMPRINT",EDGE,{"derivedFrom":subQ1}),1.0]])]});}
            var Q127;
            {var subQ1=sQuery(id+"F2.wireOp",EDGE,"E38.4.0");Q127=makeQuery(id+"F2.imprint","IMPRINT",FACE,{"disambiguationData":[TD([[makeQuery(id+"F2.imprint","IMPRINT",EDGE,{"derivedFrom":subQ1}),1.0]])]});}
            var Q128;
            {var subQ1=sQuery(id+"F2.wireOp",EDGE,"E38.129.0");Q128=makeQuery(id+"F2.imprint","IMPRINT",FACE,{"disambiguationData":[TD([[makeQuery(id+"F2.imprint","IMPRINT",EDGE,{"derivedFrom":subQ1}),1.0]])]});}
            var Q129;
            {var subQ1=sQuery(id+"F2.wireOp",EDGE,"E38.114.0");Q129=makeQuery(id+"F2.imprint","IMPRINT",FACE,{"disambiguationData":[TD([[makeQuery(id+"F2.imprint","IMPRINT",EDGE,{"derivedFrom":subQ1}),1.0]])]});}
            var Q130;
            {var subQ1=sQuery(id+"F2.wireOp",EDGE,"E38.93.0");Q130=makeQuery(id+"F2.imprint","IMPRINT",FACE,{"disambiguationData":[TD([[makeQuery(id+"F2.imprint","IMPRINT",EDGE,{"derivedFrom":subQ1}),1.0]])]});}
            var Q131;
            {var subQ1=sQuery(id+"F2.wireOp",EDGE,"E38.92.0");Q131=makeQuery(id+"F2.imprint","IMPRINT",FACE,{"disambiguationData":[TD([[makeQuery(id+"F2.imprint","IMPRINT",EDGE,{"derivedFrom":subQ1}),1.0]])]});}
            var Q132;
            {var subQ1=sQuery(id+"F2.wireOp",EDGE,"E38.91.0");Q132=makeQuery(id+"F2.imprint","IMPRINT",FACE,{"disambiguationData":[TD([[makeQuery(id+"F2.imprint","IMPRINT",EDGE,{"derivedFrom":subQ1}),1.0]])]});}
            var Q133;
            {var subQ1=sQuery(id+"F2.wireOp",EDGE,"E38.83.0");Q133=makeQuery(id+"F2.imprint","IMPRINT",FACE,{"disambiguationData":[TD([[makeQuery(id+"F2.imprint","IMPRINT",EDGE,{"derivedFrom":subQ1}),1.0]])]});}
            var Q134;
            {var subQ1=sQuery(id+"F2.wireOp",EDGE,"E38.82.0");Q134=makeQuery(id+"F2.imprint","IMPRINT",FACE,{"disambiguationData":[TD([[makeQuery(id+"F2.imprint","IMPRINT",EDGE,{"derivedFrom":subQ1}),1.0]])]});}
            var Q135;
            {var subQ1=sQuery(id+"F2.wireOp",EDGE,"E38.81.0");Q135=makeQuery(id+"F2.imprint","IMPRINT",FACE,{"disambiguationData":[TD([[makeQuery(id+"F2.imprint","IMPRINT",EDGE,{"derivedFrom":subQ1}),1.0]])]});}
            var Q136;
            {var subQ1=sQuery(id+"F2.wireOp",EDGE,"E38.77.0");Q136=makeQuery(id+"F2.imprint","IMPRINT",FACE,{"disambiguationData":[TD([[makeQuery(id+"F2.imprint","IMPRINT",EDGE,{"derivedFrom":subQ1}),1.0]])]});}
            var Q137;
            {var subQ1=sQuery(id+"F2.wireOp",EDGE,"E38.73.0");Q137=makeQuery(id+"F2.imprint","IMPRINT",FACE,{"disambiguationData":[TD([[makeQuery(id+"F2.imprint","IMPRINT",EDGE,{"derivedFrom":subQ1}),1.0]])]});}
            var Q138;
            {var subQ1=sQuery(id+"F2.wireOp",EDGE,"E38.61.0");Q138=makeQuery(id+"F2.imprint","IMPRINT",FACE,{"disambiguationData":[TD([[makeQuery(id+"F2.imprint","IMPRINT",EDGE,{"derivedFrom":subQ1}),1.0]])]});}
            var Q139;
            {var subQ1=sQuery(id+"F2.wireOp",EDGE,"E38.64.0");Q139=makeQuery(id+"F2.imprint","IMPRINT",FACE,{"disambiguationData":[TD([[makeQuery(id+"F2.imprint","IMPRINT",EDGE,{"derivedFrom":subQ1}),1.0]])]});}
            extrude(context, id + "F5", {"entities" : qUnion([Q0, Q1, Q2, Q3, Q4, Q5, Q6, Q7, Q8, Q9, Q10, Q11, Q12, Q13, Q14, Q15, Q16, Q17, Q18, Q19, Q20, Q21, Q22, Q23, Q24, Q25, Q26, Q27, Q28, Q29, Q30, Q31, Q32, Q33, Q34, Q35, Q36, Q37, Q38, Q39, Q40, Q41, Q42, Q43, Q44, Q45, Q46, Q47, Q48, Q49, Q50, Q51, Q52, Q53, Q54, Q55, Q56, Q57, Q58, Q59, Q60, Q61, Q62, Q63, Q64, Q65, Q66, Q67, Q68, Q69, Q70, Q71, Q72, Q73, Q74, Q75, Q76, Q77, Q78, Q79, Q80, Q81, Q82, Q83, Q84, Q85, Q86, Q87, Q88, Q89, Q90, Q91, Q92, Q93, Q94, Q95, Q96, Q97, Q98, Q99, Q100, Q101, Q102, Q103, Q104, Q105, Q106, Q107, Q108, Q109, Q110, Q111, Q112, Q113, Q114, Q115, Q116, Q117, Q118, Q119, Q120, Q121, Q122, Q123, Q124, Q125, Q126, Q127, Q128, Q129, Q130, Q131, Q132, Q133, Q134, Q135, Q136, Q137, Q138, Q139]), "operationType" : NewBodyOperationType.REMOVE, "endBound" : BoundingType.THROUGH_ALL, "oppositeDirection" : true, "depth" : 25 * mm});
        }
        {
            var Q0;
            Q0=makeQuery(id+"F2.imprint","IMPRINT",FACE,{"disambiguationData":[TD([[makeQuery(id+"F2.imprint","IMPRINT",EDGE,{"derivedFrom":sQuery(id+"F2.wireOp",EDGE,"E39.0")}),1.0]])]});
            extrude(context, id + "F6", {"entities" : qUnion([Q0]), "operationType" : NewBodyOperationType.REMOVE, "oppositeDirection" : true, "depth" : 33 * mm});
        }
    });
